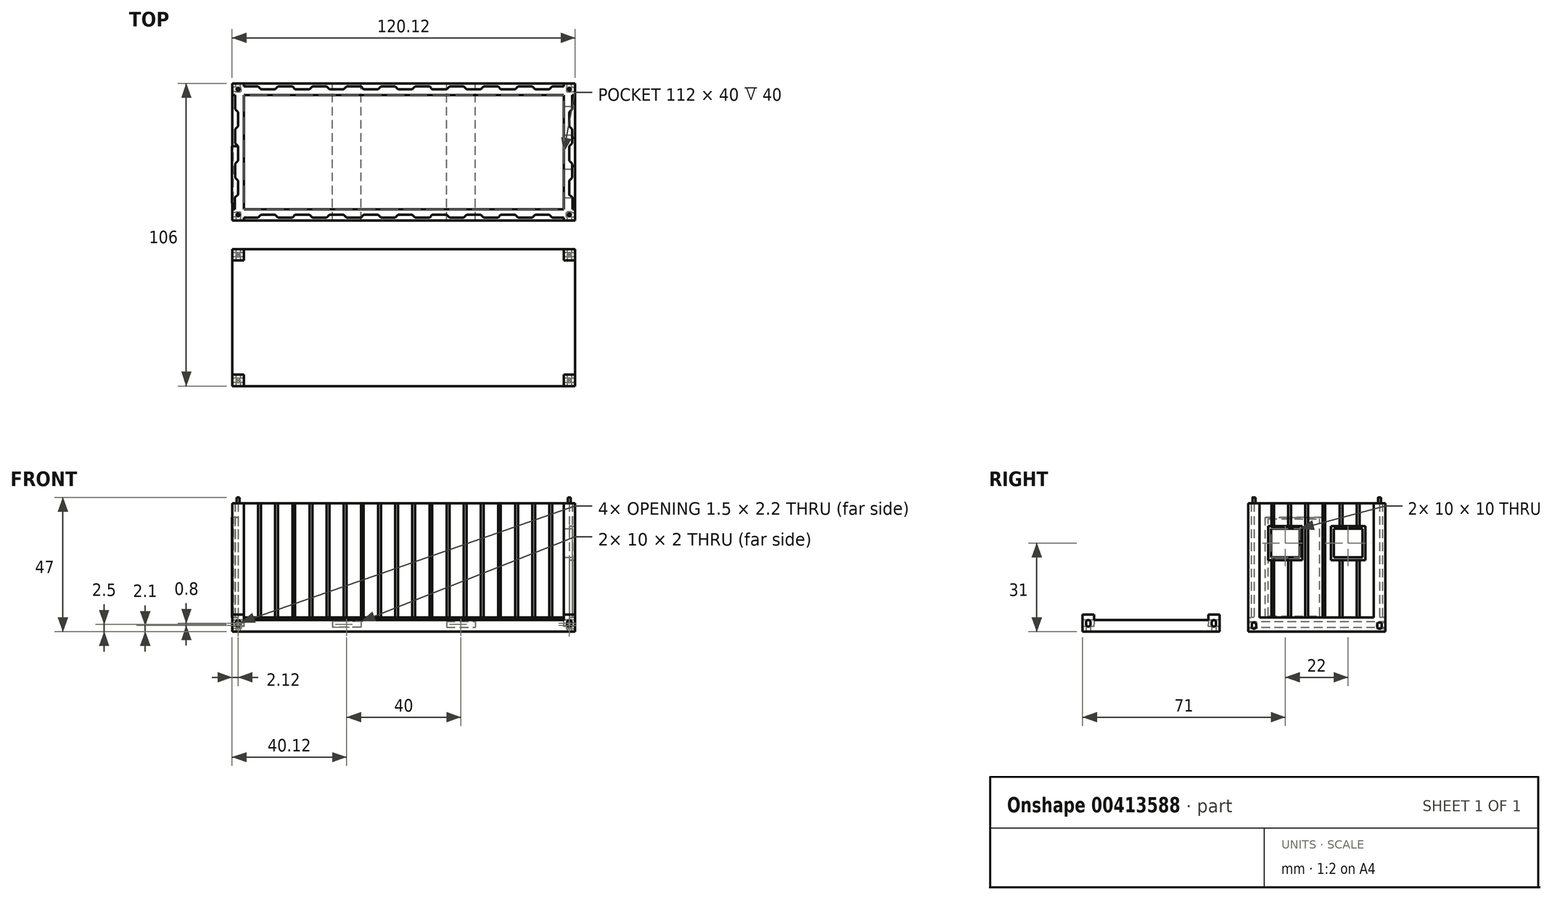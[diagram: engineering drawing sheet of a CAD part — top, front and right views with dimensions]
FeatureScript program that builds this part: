
annotation { "Feature Type Name" : "Feature", "Feature Type Description" : "" }
export const myFeature = defineFeature(function(context is Context, id is Id, definition is map)
    precondition{}
    {
        {
            var Q0;
            Q0=qCreatedBy(makeId("Top.planeOp"),FACE);
            var sketch = newSketch(context, id + "F0", { "sketchPlane" : qUnion([Q0])});
            skLineSegment(sketch, "E0.bottom", {"start": v(0, 0) * mm, "end": v(120, 0) * mm});
            skLineSegment(sketch, "E0.top", {"start": v(0, 48) * mm, "end": v(120, 48) * mm});
            skLineSegment(sketch, "E0.left", {"start": v(0, 0) * mm, "end": v(0, 48) * mm});
            skLineSegment(sketch, "E0.right", {"start": v(120, 0) * mm, "end": v(120, 48) * mm});
            skSolve(sketch);
        }
        {
            var Q0;
            Q0=makeQuery(id+"F0.imprint","IMPRINT",FACE,{"disambiguationData":[TD([[makeQuery(id+"F0.imprint","IMPRINT",EDGE,{"derivedFrom":sQuery(id+"F0.wireOp",EDGE,"E0.bottom")}),1.0]])]});
            extrude(context, id + "F1", {"entities" : qUnion([Q0]), "depth" : 5 * mm});
        }
        {
            var Q0;
            Q0=makeQuery(id+"F1.opExtrude","CAP_FACE",FACE,{"disambiguationData":[OSD([sQuery(id+"F0.wireOp",EDGE,"E0.bottom"),sQuery(id+"F0.wireOp",EDGE,"E0.top"),sQuery(id+"F0.wireOp",EDGE,"E0.left"),sQuery(id+"F0.wireOp",EDGE,"E0.right")])],"isStart":false});
            var sketch = newSketch(context, id + "F2", { "sketchPlane" : qUnion([Q0])});
            skLineSegment(sketch, "E1.bottom", {"start": v(120, 48) * mm, "end": v(116, 48) * mm});
            skLineSegment(sketch, "E1.top", {"start": v(120, 44) * mm, "end": v(119, 44) * mm});
            skLineSegment(sketch, "E1.left", {"start": v(120, 48) * mm, "end": v(120, 44) * mm});
            skLineSegment(sketch, "E1.right", {"start": v(116, 48) * mm, "end": v(116, 47) * mm});
            skLineSegment(sketch, "E2.bottom", {"start": v(120, 0) * mm, "end": v(116, 0) * mm});
            skLineSegment(sketch, "E2.top", {"start": v(120, 4) * mm, "end": v(119.12, 4) * mm});
            skLineSegment(sketch, "E2.left", {"start": v(120, 0) * mm, "end": v(120, 4) * mm});
            skLineSegment(sketch, "E2.right", {"start": v(116, 0) * mm, "end": v(116, 1) * mm});
            skLineSegment(sketch, "E3.bottom", {"start": v(0, 48) * mm, "end": v(4, 48) * mm});
            skLineSegment(sketch, "E3.top", {"start": v(0, 44) * mm, "end": v(1, 44) * mm});
            skLineSegment(sketch, "E3.left", {"start": v(0, 48) * mm, "end": v(0, 44) * mm});
            skLineSegment(sketch, "E3.right", {"start": v(4, 48) * mm, "end": v(4, 47) * mm});
            skLineSegment(sketch, "E4.bottom", {"start": v(0, 0) * mm, "end": v(4, 0) * mm});
            skLineSegment(sketch, "E4.top", {"start": v(0, 4) * mm, "end": v(0.88, 4) * mm});
            skLineSegment(sketch, "E4.left", {"start": v(0, 0) * mm, "end": v(0, 4) * mm});
            skLineSegment(sketch, "E4.right", {"start": v(4, 0) * mm, "end": v(4, 1) * mm});
            skLineSegment(sketch, "E5", {"start": v(4, 48) * mm, "end": v(4, 47) * mm, "construction": true});
            skLineSegment(sketch, "E6", {"start": v(4, 47) * mm, "end": v(9, 47) * mm});
            skLineSegment(sketch, "E7", {"start": v(9, 47) * mm, "end": v(10, 46) * mm});
            skLineSegment(sketch, "E8", {"start": v(10, 46) * mm, "end": v(15, 46) * mm});
            skLineSegment(sketch, "E9", {"start": v(15, 46) * mm, "end": v(16, 47) * mm});
            skLineSegment(sketch, "E10.1.0.0", {"start": v(16, 47) * mm, "end": v(21, 47) * mm});
            skLineSegment(sketch, "E10.1.0.1", {"start": v(21, 47) * mm, "end": v(22, 46) * mm});
            skLineSegment(sketch, "E10.1.0.2", {"start": v(27, 46) * mm, "end": v(28, 47) * mm});
            skLineSegment(sketch, "E10.2.0.0", {"start": v(28, 47) * mm, "end": v(33, 47) * mm});
            skLineSegment(sketch, "E10.2.0.1", {"start": v(33, 47) * mm, "end": v(34, 46) * mm});
            skLineSegment(sketch, "E10.2.0.2", {"start": v(39, 46) * mm, "end": v(40, 47) * mm});
            skLineSegment(sketch, "E10.3.0.0", {"start": v(40, 47) * mm, "end": v(45, 47) * mm});
            skLineSegment(sketch, "E10.3.0.1", {"start": v(45, 47) * mm, "end": v(46, 46) * mm});
            skLineSegment(sketch, "E10.3.0.2", {"start": v(51, 46) * mm, "end": v(52, 47) * mm});
            skLineSegment(sketch, "E10.4.0.0", {"start": v(52, 47) * mm, "end": v(57, 47) * mm});
            skLineSegment(sketch, "E10.4.0.1", {"start": v(57, 47) * mm, "end": v(58, 46) * mm});
            skLineSegment(sketch, "E10.4.0.2", {"start": v(63, 46) * mm, "end": v(64, 47) * mm});
            skLineSegment(sketch, "E10.5.0.0", {"start": v(64, 47) * mm, "end": v(69, 47) * mm});
            skLineSegment(sketch, "E10.5.0.1", {"start": v(69, 47) * mm, "end": v(70, 46) * mm});
            skLineSegment(sketch, "E10.5.0.2", {"start": v(75, 46) * mm, "end": v(76, 47) * mm});
            skLineSegment(sketch, "E10.6.0.0", {"start": v(76, 47) * mm, "end": v(81, 47) * mm});
            skLineSegment(sketch, "E10.6.0.1", {"start": v(81, 47) * mm, "end": v(82, 46) * mm});
            skLineSegment(sketch, "E10.6.0.2", {"start": v(87, 46) * mm, "end": v(88, 47) * mm});
            skLineSegment(sketch, "E10.7.0.0", {"start": v(88, 47) * mm, "end": v(93, 47) * mm});
            skLineSegment(sketch, "E10.7.0.1", {"start": v(93, 47) * mm, "end": v(94, 46) * mm});
            skLineSegment(sketch, "E10.7.0.2", {"start": v(99, 46) * mm, "end": v(100, 47) * mm});
            skLineSegment(sketch, "E10.8.0.0", {"start": v(100, 47) * mm, "end": v(105, 47) * mm});
            skLineSegment(sketch, "E10.8.0.1", {"start": v(105, 47) * mm, "end": v(106, 46) * mm});
            skLineSegment(sketch, "E10.8.0.2", {"start": v(111, 46) * mm, "end": v(112, 47) * mm});
            skLineSegment(sketch, "E11", {"start": v(112, 47) * mm, "end": v(116, 47) * mm});
            skLineSegment(sketch, "E12", {"start": v(22, 46) * mm, "end": v(27, 46) * mm});
            skLineSegment(sketch, "E13", {"start": v(34, 46) * mm, "end": v(39, 46) * mm});
            skLineSegment(sketch, "E14", {"start": v(46, 46) * mm, "end": v(51, 46) * mm});
            skLineSegment(sketch, "E15", {"start": v(58, 46) * mm, "end": v(63, 46) * mm});
            skLineSegment(sketch, "E16", {"start": v(70, 46) * mm, "end": v(75, 46) * mm});
            skLineSegment(sketch, "E17", {"start": v(82, 46) * mm, "end": v(87, 46) * mm});
            skLineSegment(sketch, "E18", {"start": v(94, 46) * mm, "end": v(99, 46) * mm});
            skLineSegment(sketch, "E19", {"start": v(106, 46) * mm, "end": v(111, 46) * mm});
            skLineSegment(sketch, "E20", {"start": v(4, 44) * mm, "end": v(116, 44) * mm});
            skLineSegment(sketch, "E21.MirrorCS", {"start": v(4, 1) * mm, "end": v(9, 1) * mm});
            skLineSegment(sketch, "E22.MirrorCS", {"start": v(9, 1) * mm, "end": v(10, 2) * mm});
            skLineSegment(sketch, "E23.MirrorCS", {"start": v(10, 2) * mm, "end": v(15, 2) * mm});
            skLineSegment(sketch, "E24.MirrorCS", {"start": v(15, 2) * mm, "end": v(16, 1) * mm});
            skLineSegment(sketch, "E25.MirrorCS", {"start": v(16, 1) * mm, "end": v(21, 1) * mm});
            skLineSegment(sketch, "E26.MirrorCS", {"start": v(21, 1) * mm, "end": v(22, 2) * mm});
            skLineSegment(sketch, "E27.MirrorCS", {"start": v(22, 2) * mm, "end": v(27, 2) * mm});
            skLineSegment(sketch, "E28.MirrorCS", {"start": v(27, 2) * mm, "end": v(28, 1) * mm});
            skLineSegment(sketch, "E29.MirrorCS", {"start": v(28, 1) * mm, "end": v(33, 1) * mm});
            skLineSegment(sketch, "E30.MirrorCS", {"start": v(33, 1) * mm, "end": v(34, 2) * mm});
            skLineSegment(sketch, "E31.MirrorCS", {"start": v(34, 2) * mm, "end": v(39, 2) * mm});
            skLineSegment(sketch, "E32.MirrorCS", {"start": v(39, 2) * mm, "end": v(40, 1) * mm});
            skLineSegment(sketch, "E33.MirrorCS", {"start": v(40, 1) * mm, "end": v(45, 1) * mm});
            skLineSegment(sketch, "E34.MirrorCS", {"start": v(45, 1) * mm, "end": v(46, 2) * mm});
            skLineSegment(sketch, "E35.MirrorCS", {"start": v(46, 2) * mm, "end": v(51, 2) * mm});
            skLineSegment(sketch, "E36.MirrorCS", {"start": v(51, 2) * mm, "end": v(52, 1) * mm});
            skLineSegment(sketch, "E37.MirrorCS", {"start": v(52, 1) * mm, "end": v(57, 1) * mm});
            skLineSegment(sketch, "E38.MirrorCS", {"start": v(57, 1) * mm, "end": v(58, 2) * mm});
            skLineSegment(sketch, "E39.MirrorCS", {"start": v(58, 2) * mm, "end": v(63, 2) * mm});
            skLineSegment(sketch, "E40.MirrorCS", {"start": v(63, 2) * mm, "end": v(64, 1) * mm});
            skLineSegment(sketch, "E41.MirrorCS", {"start": v(64, 1) * mm, "end": v(69, 1) * mm});
            skLineSegment(sketch, "E42.MirrorCS", {"start": v(69, 1) * mm, "end": v(70, 2) * mm});
            skLineSegment(sketch, "E43.MirrorCS", {"start": v(70, 2) * mm, "end": v(75, 2) * mm});
            skLineSegment(sketch, "E44.MirrorCS", {"start": v(75, 2) * mm, "end": v(76, 1) * mm});
            skLineSegment(sketch, "E45.MirrorCS", {"start": v(76, 1) * mm, "end": v(81, 1) * mm});
            skLineSegment(sketch, "E46.MirrorCS", {"start": v(81, 1) * mm, "end": v(82, 2) * mm});
            skLineSegment(sketch, "E47.MirrorCS", {"start": v(82, 2) * mm, "end": v(87, 2) * mm});
            skLineSegment(sketch, "E48.MirrorCS", {"start": v(87, 2) * mm, "end": v(88, 1) * mm});
            skLineSegment(sketch, "E49.MirrorCS", {"start": v(88, 1) * mm, "end": v(93, 1) * mm});
            skLineSegment(sketch, "E50.MirrorCS", {"start": v(93, 1) * mm, "end": v(94, 2) * mm});
            skLineSegment(sketch, "E51.MirrorCS", {"start": v(94, 2) * mm, "end": v(99, 2) * mm});
            skLineSegment(sketch, "E52.MirrorCS", {"start": v(99, 2) * mm, "end": v(100, 1) * mm});
            skLineSegment(sketch, "E53.MirrorCS", {"start": v(100, 1) * mm, "end": v(105, 1) * mm});
            skLineSegment(sketch, "E54.MirrorCS", {"start": v(105, 1) * mm, "end": v(106, 2) * mm});
            skLineSegment(sketch, "E55.MirrorCS", {"start": v(106, 2) * mm, "end": v(111, 2) * mm});
            skLineSegment(sketch, "E56.MirrorCS", {"start": v(111, 2) * mm, "end": v(112, 1) * mm});
            skLineSegment(sketch, "E57.MirrorCS", {"start": v(112, 1) * mm, "end": v(116, 1) * mm});
            skLineSegment(sketch, "E58", {"start": v(4, 4) * mm, "end": v(116, 4) * mm});
            skLineSegment(sketch, "E59", {"start": v(0, 44) * mm, "end": v(1, 44) * mm, "construction": true});
            skLineSegment(sketch, "E60", {"start": v(1, 44) * mm, "end": v(1, 39) * mm});
            skLineSegment(sketch, "E61", {"start": v(1, 39) * mm, "end": v(2, 38) * mm});
            skLineSegment(sketch, "E62", {"start": v(2, 38) * mm, "end": v(2, 33) * mm});
            skLineSegment(sketch, "E63", {"start": v(2, 33) * mm, "end": v(1, 32) * mm});
            skLineSegment(sketch, "E64", {"start": v(1, 32) * mm, "end": v(1, 27) * mm});
            skLineSegment(sketch, "E65", {"start": v(1, 27) * mm, "end": v(2, 26) * mm});
            skLineSegment(sketch, "E66", {"start": v(2, 26) * mm, "end": v(2, 21) * mm});
            skLineSegment(sketch, "E67", {"start": v(2, 21) * mm, "end": v(1, 20) * mm});
            skLineSegment(sketch, "E68", {"start": v(1, 20) * mm, "end": v(1, 15) * mm});
            skLineSegment(sketch, "E69", {"start": v(1, 15) * mm, "end": v(2.02, 13.98) * mm});
            skLineSegment(sketch, "E70", {"start": v(2.02, 13.98) * mm, "end": v(2.02, 8.98) * mm});
            skLineSegment(sketch, "E71", {"start": v(2.02, 8.98) * mm, "end": v(0.88, 8.1) * mm});
            skLineSegment(sketch, "E72", {"start": v(0.88, 8.1) * mm, "end": v(0.88, 4) * mm});
            skLineSegment(sketch, "E73.MirrorCS", {"start": v(119.12, 8.1) * mm, "end": v(119.12, 4) * mm});
            skLineSegment(sketch, "E74.MirrorCS", {"start": v(117.98, 8.98) * mm, "end": v(119.12, 8.1) * mm});
            skLineSegment(sketch, "E75.MirrorCS", {"start": v(117.98, 13.98) * mm, "end": v(117.98, 8.98) * mm});
            skLineSegment(sketch, "E76.MirrorCS", {"start": v(119, 15) * mm, "end": v(117.98, 13.98) * mm});
            skLineSegment(sketch, "E77.MirrorCS", {"start": v(119, 20) * mm, "end": v(119, 15) * mm});
            skLineSegment(sketch, "E78.MirrorCS", {"start": v(118, 21) * mm, "end": v(119, 20) * mm});
            skLineSegment(sketch, "E79.MirrorCS", {"start": v(118, 26) * mm, "end": v(118, 21) * mm});
            skLineSegment(sketch, "E80.MirrorCS", {"start": v(119, 32) * mm, "end": v(119, 27) * mm});
            skLineSegment(sketch, "E81.MirrorCS", {"start": v(118, 33) * mm, "end": v(119, 32) * mm});
            skLineSegment(sketch, "E82.MirrorCS", {"start": v(118, 38) * mm, "end": v(118, 33) * mm});
            skLineSegment(sketch, "E83.MirrorCS", {"start": v(119, 39) * mm, "end": v(118, 38) * mm});
            skLineSegment(sketch, "E84.MirrorCS", {"start": v(119, 44) * mm, "end": v(119, 39) * mm});
            skLineSegment(sketch, "E85.MirrorCS", {"start": v(119, 27) * mm, "end": v(118, 26) * mm});
            skLineSegment(sketch, "E86", {"start": v(4, 44) * mm, "end": v(4, 4) * mm});
            skLineSegment(sketch, "E87", {"start": v(116, 4) * mm, "end": v(116, 44) * mm});
            skPoint(sketch, "E88.orphan", {"position": v(4, 46) * mm});
            skPoint(sketch, "E89.orphan", {"position": v(2, 44) * mm});
            skSolve(sketch);
        }
        {
            var Q0;
            Q0 = qSketchRegion(id + "F2", true);
            extrude(context, id + "F3", {"entities" : qUnion([Q0]), "operationType" : NewBodyOperationType.ADD, "depth" : 40 * mm});
        }
        {
            var Q0;
            Q0=makeQuery(id+"F3.opExtrude","CAP_FACE",FACE,{"disambiguationData":[OSD([sQuery(id+"F2.wireOp",EDGE,"E1.bottom"),sQuery(id+"F2.wireOp",EDGE,"E1.top"),sQuery(id+"F2.wireOp",EDGE,"E1.left"),sQuery(id+"F2.wireOp",EDGE,"E1.right"),sQuery(id+"F2.wireOp",EDGE,"E2.bottom"),sQuery(id+"F2.wireOp",EDGE,"E2.top"),sQuery(id+"F2.wireOp",EDGE,"E2.left"),sQuery(id+"F2.wireOp",EDGE,"E2.right"),sQuery(id+"F2.wireOp",EDGE,"E3.bottom"),sQuery(id+"F2.wireOp",EDGE,"E3.top"),sQuery(id+"F2.wireOp",EDGE,"E3.left"),sQuery(id+"F2.wireOp",EDGE,"E3.right"),sQuery(id+"F2.wireOp",EDGE,"E4.bottom"),sQuery(id+"F2.wireOp",EDGE,"E4.top"),sQuery(id+"F2.wireOp",EDGE,"E4.left"),sQuery(id+"F2.wireOp",EDGE,"E4.right"),sQuery(id+"F2.wireOp",EDGE,"E6"),sQuery(id+"F2.wireOp",EDGE,"E7"),sQuery(id+"F2.wireOp",EDGE,"E8"),sQuery(id+"F2.wireOp",EDGE,"E9"),sQuery(id+"F2.wireOp",EDGE,"E10.1.0.0"),sQuery(id+"F2.wireOp",EDGE,"E10.1.0.1"),sQuery(id+"F2.wireOp",EDGE,"E10.1.0.2"),sQuery(id+"F2.wireOp",EDGE,"E10.2.0.0"),sQuery(id+"F2.wireOp",EDGE,"E10.2.0.1"),sQuery(id+"F2.wireOp",EDGE,"E10.2.0.2"),sQuery(id+"F2.wireOp",EDGE,"E10.3.0.0"),sQuery(id+"F2.wireOp",EDGE,"E10.3.0.1"),sQuery(id+"F2.wireOp",EDGE,"E10.3.0.2"),sQuery(id+"F2.wireOp",EDGE,"E10.4.0.0"),sQuery(id+"F2.wireOp",EDGE,"E10.4.0.1"),sQuery(id+"F2.wireOp",EDGE,"E10.4.0.2"),sQuery(id+"F2.wireOp",EDGE,"E10.5.0.0"),sQuery(id+"F2.wireOp",EDGE,"E10.5.0.1"),sQuery(id+"F2.wireOp",EDGE,"E10.5.0.2"),sQuery(id+"F2.wireOp",EDGE,"E10.6.0.0"),sQuery(id+"F2.wireOp",EDGE,"E10.6.0.1"),sQuery(id+"F2.wireOp",EDGE,"E10.6.0.2"),sQuery(id+"F2.wireOp",EDGE,"E10.7.0.0"),sQuery(id+"F2.wireOp",EDGE,"E10.7.0.1"),sQuery(id+"F2.wireOp",EDGE,"E10.7.0.2"),sQuery(id+"F2.wireOp",EDGE,"E10.8.0.0"),sQuery(id+"F2.wireOp",EDGE,"E10.8.0.1"),sQuery(id+"F2.wireOp",EDGE,"E10.8.0.2"),sQuery(id+"F2.wireOp",EDGE,"E11"),sQuery(id+"F2.wireOp",EDGE,"E12"),sQuery(id+"F2.wireOp",EDGE,"E13"),sQuery(id+"F2.wireOp",EDGE,"E14"),sQuery(id+"F2.wireOp",EDGE,"E15"),sQuery(id+"F2.wireOp",EDGE,"E16"),sQuery(id+"F2.wireOp",EDGE,"E17"),sQuery(id+"F2.wireOp",EDGE,"E18"),sQuery(id+"F2.wireOp",EDGE,"E19"),sQuery(id+"F2.wireOp",EDGE,"E20"),sQuery(id+"F2.wireOp",EDGE,"E21.MirrorCS"),sQuery(id+"F2.wireOp",EDGE,"E22.MirrorCS"),sQuery(id+"F2.wireOp",EDGE,"E23.MirrorCS"),sQuery(id+"F2.wireOp",EDGE,"E24.MirrorCS"),sQuery(id+"F2.wireOp",EDGE,"E25.MirrorCS"),sQuery(id+"F2.wireOp",EDGE,"E26.MirrorCS"),sQuery(id+"F2.wireOp",EDGE,"E27.MirrorCS"),sQuery(id+"F2.wireOp",EDGE,"E28.MirrorCS"),sQuery(id+"F2.wireOp",EDGE,"E29.MirrorCS"),sQuery(id+"F2.wireOp",EDGE,"E30.MirrorCS"),sQuery(id+"F2.wireOp",EDGE,"E31.MirrorCS"),sQuery(id+"F2.wireOp",EDGE,"E32.MirrorCS"),sQuery(id+"F2.wireOp",EDGE,"E33.MirrorCS"),sQuery(id+"F2.wireOp",EDGE,"E34.MirrorCS"),sQuery(id+"F2.wireOp",EDGE,"E35.MirrorCS"),sQuery(id+"F2.wireOp",EDGE,"E36.MirrorCS"),sQuery(id+"F2.wireOp",EDGE,"E37.MirrorCS"),sQuery(id+"F2.wireOp",EDGE,"E38.MirrorCS"),sQuery(id+"F2.wireOp",EDGE,"E39.MirrorCS"),sQuery(id+"F2.wireOp",EDGE,"E40.MirrorCS"),sQuery(id+"F2.wireOp",EDGE,"E41.MirrorCS"),sQuery(id+"F2.wireOp",EDGE,"E42.MirrorCS"),sQuery(id+"F2.wireOp",EDGE,"E43.MirrorCS"),sQuery(id+"F2.wireOp",EDGE,"E44.MirrorCS"),sQuery(id+"F2.wireOp",EDGE,"E45.MirrorCS"),sQuery(id+"F2.wireOp",EDGE,"E46.MirrorCS"),sQuery(id+"F2.wireOp",EDGE,"E47.MirrorCS"),sQuery(id+"F2.wireOp",EDGE,"E48.MirrorCS"),sQuery(id+"F2.wireOp",EDGE,"E49.MirrorCS"),sQuery(id+"F2.wireOp",EDGE,"E50.MirrorCS"),sQuery(id+"F2.wireOp",EDGE,"E51.MirrorCS"),sQuery(id+"F2.wireOp",EDGE,"E52.MirrorCS"),sQuery(id+"F2.wireOp",EDGE,"E53.MirrorCS"),sQuery(id+"F2.wireOp",EDGE,"E54.MirrorCS"),sQuery(id+"F2.wireOp",EDGE,"E55.MirrorCS"),sQuery(id+"F2.wireOp",EDGE,"E56.MirrorCS"),sQuery(id+"F2.wireOp",EDGE,"E57.MirrorCS"),sQuery(id+"F2.wireOp",EDGE,"E58"),sQuery(id+"F2.wireOp",EDGE,"E60"),sQuery(id+"F2.wireOp",EDGE,"E61"),sQuery(id+"F2.wireOp",EDGE,"E62"),sQuery(id+"F2.wireOp",EDGE,"E63"),sQuery(id+"F2.wireOp",EDGE,"E64"),sQuery(id+"F2.wireOp",EDGE,"E65"),sQuery(id+"F2.wireOp",EDGE,"E66"),sQuery(id+"F2.wireOp",EDGE,"E67"),sQuery(id+"F2.wireOp",EDGE,"E68"),sQuery(id+"F2.wireOp",EDGE,"E69"),sQuery(id+"F2.wireOp",EDGE,"E70"),sQuery(id+"F2.wireOp",EDGE,"E71"),sQuery(id+"F2.wireOp",EDGE,"E72"),sQuery(id+"F2.wireOp",EDGE,"E73.MirrorCS"),sQuery(id+"F2.wireOp",EDGE,"E74.MirrorCS"),sQuery(id+"F2.wireOp",EDGE,"E75.MirrorCS"),sQuery(id+"F2.wireOp",EDGE,"E76.MirrorCS"),sQuery(id+"F2.wireOp",EDGE,"E77.MirrorCS"),sQuery(id+"F2.wireOp",EDGE,"E78.MirrorCS"),sQuery(id+"F2.wireOp",EDGE,"E79.MirrorCS"),sQuery(id+"F2.wireOp",EDGE,"E80.MirrorCS"),sQuery(id+"F2.wireOp",EDGE,"E81.MirrorCS"),sQuery(id+"F2.wireOp",EDGE,"E82.MirrorCS"),sQuery(id+"F2.wireOp",EDGE,"E83.MirrorCS"),sQuery(id+"F2.wireOp",EDGE,"E84.MirrorCS"),sQuery(id+"F2.wireOp",EDGE,"E85.MirrorCS"),sQuery(id+"F2.wireOp",EDGE,"E86"),sQuery(id+"F2.wireOp",EDGE,"E87")])],"isStart":false});
            var sketch = newSketch(context, id + "F4", { "sketchPlane" : qUnion([Q0])});
            skLineSegment(sketch, "E90.bottom", {"start": v(0, 0) * mm, "end": v(120, 0) * mm});
            skLineSegment(sketch, "E90.top", {"start": v(0, 48) * mm, "end": v(120, 48) * mm});
            skLineSegment(sketch, "E90.left", {"start": v(0, 0) * mm, "end": v(0, 48) * mm});
            skLineSegment(sketch, "E90.right", {"start": v(120, 0) * mm, "end": v(120, 48) * mm});
            skSolve(sketch);
        }
        {
            var Q0;
            Q0 = qSketchRegion(id + "F4", true);
            extrude(context, id + "F5", {"entities" : qUnion([Q0]), "operationType" : NewBodyOperationType.ADD, "depth" : 3 * mm});
        }
        {
            var Q0;
            Q0=makeQuery(id+"F5.opExtrude","CAP_FACE",FACE,{"disambiguationData":[OSD([sQuery(id+"F4.wireOp",EDGE,"E90.bottom"),sQuery(id+"F4.wireOp",EDGE,"E90.top"),sQuery(id+"F4.wireOp",EDGE,"E90.left"),sQuery(id+"F4.wireOp",EDGE,"E90.right")])],"isStart":false});
            var sketch = newSketch(context, id + "F6", { "sketchPlane" : qUnion([Q0])});
            skLineSegment(sketch, "E91.bottom", {"start": v(0, 48) * mm, "end": v(4, 48) * mm});
            skLineSegment(sketch, "E91.top", {"start": v(0, 44) * mm, "end": v(4, 44) * mm});
            skLineSegment(sketch, "E91.left", {"start": v(0, 48) * mm, "end": v(0, 44) * mm});
            skLineSegment(sketch, "E91.right", {"start": v(4, 48) * mm, "end": v(4, 44) * mm});
            skLineSegment(sketch, "E92.bottom", {"start": v(0, 0) * mm, "end": v(4, 0) * mm});
            skLineSegment(sketch, "E92.top", {"start": v(0, 4) * mm, "end": v(4, 4) * mm});
            skLineSegment(sketch, "E92.left", {"start": v(0, 0) * mm, "end": v(0, 4) * mm});
            skLineSegment(sketch, "E92.right", {"start": v(4, 0) * mm, "end": v(4, 4) * mm});
            skLineSegment(sketch, "E93.bottom", {"start": v(120, 48) * mm, "end": v(116, 48) * mm});
            skLineSegment(sketch, "E93.top", {"start": v(120, 44) * mm, "end": v(116, 44) * mm});
            skLineSegment(sketch, "E93.left", {"start": v(120, 48) * mm, "end": v(120, 44) * mm});
            skLineSegment(sketch, "E93.right", {"start": v(116, 48) * mm, "end": v(116, 44) * mm});
            skLineSegment(sketch, "E94.bottom", {"start": v(120, 0) * mm, "end": v(116, 0) * mm});
            skLineSegment(sketch, "E94.top", {"start": v(120, 4) * mm, "end": v(116, 4) * mm});
            skLineSegment(sketch, "E94.left", {"start": v(120, 0) * mm, "end": v(120, 4) * mm});
            skLineSegment(sketch, "E94.right", {"start": v(116, 0) * mm, "end": v(116, 4) * mm});
            skSolve(sketch);
        }
        {
            var Q0;
            Q0 = qSketchRegion(id + "F6", true);
            extrude(context, id + "F7", {"entities" : qUnion([Q0]), "operationType" : NewBodyOperationType.ADD, "depth" : 2 * mm});
        }
        {
            var Q0;
            Q0=makeQuery(id+"F7.boolean.opBoolean","MERGE",FACE,{"derivedFrom":[makeQuery(id+"F5.boolean.opBoolean","MERGE",FACE,{"derivedFrom":[makeQuery(id+"F3.boolean.opBoolean","MERGE",FACE,{"derivedFrom":[makeQuery(id+"F1.opExtrude","SWEPT_FACE",FACE,{"disambiguationData":[OSD([sQuery(id+"F0.wireOp",EDGE,"E0.bottom")])]}),makeQuery(id+"F3.opExtrude","SWEPT_FACE",FACE,{"disambiguationData":[OSD([sQuery(id+"F2.wireOp",EDGE,"E2.bottom")])]}),makeQuery(id+"F3.opExtrude","SWEPT_FACE",FACE,{"disambiguationData":[OSD([sQuery(id+"F2.wireOp",EDGE,"E4.bottom")])]})]}),makeQuery(id+"F5.opExtrude","SWEPT_FACE",FACE,{"disambiguationData":[OSD([sQuery(id+"F4.wireOp",EDGE,"E90.bottom")])]})]}),makeQuery(id+"F7.opExtrude","SWEPT_FACE",FACE,{"disambiguationData":[OSD([sQuery(id+"F6.wireOp",EDGE,"E92.bottom")])]}),makeQuery(id+"F7.opExtrude","SWEPT_FACE",FACE,{"disambiguationData":[OSD([sQuery(id+"F6.wireOp",EDGE,"E94.bottom")])]})]});
            var sketch = newSketch(context, id + "F8", { "sketchPlane" : qUnion([Q0])});
            skLineSegment(sketch, "E95", {"start": v(2, 50) * mm, "end": v(1.25, 50) * mm, "construction": true});
            skLineSegment(sketch, "E96", {"start": v(1.25, 50) * mm, "end": v(1.25, 49) * mm, "construction": true});
            skLineSegment(sketch, "E97.bottom", {"start": v(1.95, 49) * mm, "end": v(2.05, 49) * mm});
            skLineSegment(sketch, "E97.top", {"start": v(1.95, 46.8) * mm, "end": v(2.05, 46.8) * mm});
            skLineSegment(sketch, "E97.left", {"start": v(1.25, 48.3) * mm, "end": v(1.25, 47.5) * mm});
            skLineSegment(sketch, "E97.right", {"start": v(2.75, 48.3) * mm, "end": v(2.75, 47.5) * mm});
            skPoint(sketch, "E98.visualSharp", {"position": v(1.25, 49) * mm});
            skArc(sketch, "E98.filletArc", {"start": v(1.95, 49) * mm, "mid": v(1.46, 48.8) * mm, "end": v(1.25, 48.3) * mm});
            skPoint(sketch, "E99.visualSharp", {"position": v(2.75, 49) * mm});
            skArc(sketch, "E99.filletArc", {"start": v(2.75, 48.3) * mm, "mid": v(2.54, 48.8) * mm, "end": v(2.05, 49) * mm});
            skPoint(sketch, "E100.visualSharp", {"position": v(1.25, 46.8) * mm});
            skArc(sketch, "E100.filletArc", {"start": v(1.25, 47.5) * mm, "mid": v(1.46, 47) * mm, "end": v(1.95, 46.8) * mm});
            skPoint(sketch, "E101.visualSharp", {"position": v(2.75, 46.8) * mm});
            skArc(sketch, "E101.filletArc", {"start": v(2.05, 46.8) * mm, "mid": v(2.54, 47) * mm, "end": v(2.75, 47.5) * mm});
            skLineSegment(sketch, "E102", {"start": v(60, 48) * mm, "end": v(60, 62.26) * mm, "construction": true});
            skPoint(sketch, "E102.endSnap0", {"position": v(60, 45) * mm});
            skArc(sketch, "E103.MirrorCS", {"start": v(118.05, 49) * mm, "mid": v(118.54, 48.8) * mm, "end": v(118.75, 48.3) * mm});
            skLineSegment(sketch, "E104.MirrorCS", {"start": v(118.05, 49) * mm, "end": v(117.95, 49) * mm});
            skArc(sketch, "E105.MirrorCS", {"start": v(117.25, 48.3) * mm, "mid": v(117.46, 48.8) * mm, "end": v(117.95, 49) * mm});
            skLineSegment(sketch, "E106.MirrorCS", {"start": v(118.75, 48.3) * mm, "end": v(118.75, 47.5) * mm});
            skArc(sketch, "E107.MirrorCS", {"start": v(118.75, 47.5) * mm, "mid": v(118.54, 47) * mm, "end": v(118.05, 46.8) * mm});
            skLineSegment(sketch, "E108.MirrorCS", {"start": v(117.25, 48.3) * mm, "end": v(117.25, 47.5) * mm});
            skArc(sketch, "E109.MirrorCS", {"start": v(117.95, 46.8) * mm, "mid": v(117.46, 47) * mm, "end": v(117.25, 47.5) * mm});
            skLineSegment(sketch, "E110.MirrorCS", {"start": v(118.05, 46.8) * mm, "end": v(117.95, 46.8) * mm});
            skLineSegment(sketch, "E111", {"start": v(0, 25) * mm, "end": v(-2.77, 25) * mm, "construction": true});
            skLineSegment(sketch, "E112.MirrorCS", {"start": v(1.25, 1.7) * mm, "end": v(1.25, 2.5) * mm});
            skArc(sketch, "E113.MirrorCS", {"start": v(1.95, 1) * mm, "mid": v(1.46, 1.2) * mm, "end": v(1.25, 1.7) * mm});
            skLineSegment(sketch, "E114.MirrorCS", {"start": v(1.95, 1) * mm, "end": v(2.05, 1) * mm});
            skArc(sketch, "E115.MirrorCS", {"start": v(2.75, 1.7) * mm, "mid": v(2.54, 1.2) * mm, "end": v(2.05, 1) * mm});
            skArc(sketch, "E116.MirrorCS", {"start": v(2.05, 3.2) * mm, "mid": v(2.54, 3) * mm, "end": v(2.75, 2.5) * mm});
            skLineSegment(sketch, "E117.MirrorCS", {"start": v(1.95, 3.2) * mm, "end": v(2.05, 3.2) * mm});
            skArc(sketch, "E118.MirrorCS", {"start": v(1.25, 2.5) * mm, "mid": v(1.46, 3) * mm, "end": v(1.95, 3.2) * mm});
            skLineSegment(sketch, "E119.MirrorCS", {"start": v(2.75, 1.7) * mm, "end": v(2.75, 2.5) * mm});
            skLineSegment(sketch, "E120.MirrorCS", {"start": v(117.25, 1.7) * mm, "end": v(117.25, 2.5) * mm});
            skArc(sketch, "E121.MirrorCS", {"start": v(117.25, 1.7) * mm, "mid": v(117.46, 1.2) * mm, "end": v(117.95, 1) * mm});
            skLineSegment(sketch, "E122.MirrorCS", {"start": v(118.05, 1) * mm, "end": v(117.95, 1) * mm});
            skArc(sketch, "E123.MirrorCS", {"start": v(118.05, 1) * mm, "mid": v(118.54, 1.2) * mm, "end": v(118.75, 1.7) * mm});
            skLineSegment(sketch, "E124.MirrorCS", {"start": v(118.75, 1.7) * mm, "end": v(118.75, 2.5) * mm});
            skArc(sketch, "E125.MirrorCS", {"start": v(118.75, 2.5) * mm, "mid": v(118.54, 3) * mm, "end": v(118.05, 3.2) * mm});
            skLineSegment(sketch, "E126.MirrorCS", {"start": v(118.05, 3.2) * mm, "end": v(117.95, 3.2) * mm});
            skArc(sketch, "E127.MirrorCS", {"start": v(117.95, 3.2) * mm, "mid": v(117.46, 3) * mm, "end": v(117.25, 2.5) * mm});
            skSolve(sketch);
        }
        {
            var Q0;
            Q0 = qSketchRegion(id + "F8", true);
            extrude(context, id + "F9", {"entities" : qUnion([Q0]), "operationType" : NewBodyOperationType.REMOVE, "oppositeDirection" : true, "depth" : 3 * mm});
        }
        {
            var Q0;
            Q0=makeQuery(id+"F7.boolean.opBoolean","MERGE",FACE,{"derivedFrom":[makeQuery(id+"F5.boolean.opBoolean","MERGE",FACE,{"derivedFrom":[makeQuery(id+"F3.boolean.opBoolean","MERGE",FACE,{"derivedFrom":[makeQuery(id+"F1.opExtrude","SWEPT_FACE",FACE,{"disambiguationData":[OSD([sQuery(id+"F0.wireOp",EDGE,"E0.right")])]}),makeQuery(id+"F3.opExtrude","SWEPT_FACE",FACE,{"disambiguationData":[OSD([sQuery(id+"F2.wireOp",EDGE,"E1.left")])]}),makeQuery(id+"F3.opExtrude","SWEPT_FACE",FACE,{"disambiguationData":[OSD([sQuery(id+"F2.wireOp",EDGE,"E2.left")])]})]}),makeQuery(id+"F5.opExtrude","SWEPT_FACE",FACE,{"disambiguationData":[OSD([sQuery(id+"F4.wireOp",EDGE,"E90.right")])]})]}),makeQuery(id+"F7.opExtrude","SWEPT_FACE",FACE,{"disambiguationData":[OSD([sQuery(id+"F6.wireOp",EDGE,"E93.left")])]}),makeQuery(id+"F7.opExtrude","SWEPT_FACE",FACE,{"disambiguationData":[OSD([sQuery(id+"F6.wireOp",EDGE,"E94.left")])]})]});
            var sketch = newSketch(context, id + "F10", { "sketchPlane" : qUnion([Q0])});
            skLineSegment(sketch, "E128", {"start": v(2, 50) * mm, "end": v(2, 49) * mm, "construction": true});
            skLineSegment(sketch, "E129", {"start": v(2, 49) * mm, "end": v(1.95, 49) * mm, "construction": true});
            skLineSegment(sketch, "E130.bottom", {"start": v(1.95, 49) * mm, "end": v(2.05, 49) * mm});
            skLineSegment(sketch, "E130.top", {"start": v(1.95, 46.8) * mm, "end": v(2.05, 46.8) * mm});
            skLineSegment(sketch, "E130.left", {"start": v(1.25, 48.3) * mm, "end": v(1.25, 47.5) * mm});
            skLineSegment(sketch, "E130.right", {"start": v(2.75, 48.3) * mm, "end": v(2.75, 47.5) * mm});
            skPoint(sketch, "E131.visualSharp", {"position": v(1.25, 49) * mm});
            skArc(sketch, "E131.filletArc", {"start": v(1.95, 49) * mm, "mid": v(1.46, 48.8) * mm, "end": v(1.25, 48.3) * mm});
            skPoint(sketch, "E132.visualSharp", {"position": v(2.75, 49) * mm});
            skArc(sketch, "E132.filletArc", {"start": v(2.75, 48.3) * mm, "mid": v(2.54, 48.8) * mm, "end": v(2.05, 49) * mm});
            skPoint(sketch, "E133.visualSharp", {"position": v(2.75, 46.8) * mm});
            skArc(sketch, "E133.filletArc", {"start": v(2.05, 46.8) * mm, "mid": v(2.54, 47) * mm, "end": v(2.75, 47.5) * mm});
            skPoint(sketch, "E134.visualSharp", {"position": v(1.25, 46.8) * mm});
            skArc(sketch, "E134.filletArc", {"start": v(1.25, 47.5) * mm, "mid": v(1.46, 47) * mm, "end": v(1.95, 46.8) * mm});
            skLineSegment(sketch, "E135", {"start": v(24, 48) * mm, "end": v(24, 52.07) * mm, "construction": true});
            skArc(sketch, "E136.MirrorCS", {"start": v(45.25, 48.3) * mm, "mid": v(45.46, 48.8) * mm, "end": v(45.95, 49) * mm});
            skLineSegment(sketch, "E137.MirrorCS", {"start": v(46.05, 49) * mm, "end": v(45.95, 49) * mm});
            skArc(sketch, "E138.MirrorCS", {"start": v(46.05, 49) * mm, "mid": v(46.54, 48.8) * mm, "end": v(46.75, 48.3) * mm});
            skLineSegment(sketch, "E139.MirrorCS", {"start": v(46.75, 48.3) * mm, "end": v(46.75, 47.5) * mm});
            skArc(sketch, "E140.MirrorCS", {"start": v(46.75, 47.5) * mm, "mid": v(46.54, 47) * mm, "end": v(46.05, 46.8) * mm});
            skLineSegment(sketch, "E141.MirrorCS", {"start": v(46.05, 46.8) * mm, "end": v(45.95, 46.8) * mm});
            skArc(sketch, "E142.MirrorCS", {"start": v(45.95, 46.8) * mm, "mid": v(45.46, 47) * mm, "end": v(45.25, 47.5) * mm});
            skLineSegment(sketch, "E143.MirrorCS", {"start": v(45.25, 48.3) * mm, "end": v(45.25, 47.5) * mm});
            skLineSegment(sketch, "E144", {"start": v(0, 25) * mm, "end": v(-7.52, 25) * mm, "construction": true});
            skArc(sketch, "E145.MirrorCS", {"start": v(1.95, 1) * mm, "mid": v(1.46, 1.2) * mm, "end": v(1.25, 1.7) * mm});
            skLineSegment(sketch, "E146.MirrorCS", {"start": v(1.95, 1) * mm, "end": v(2.05, 1) * mm});
            skArc(sketch, "E147.MirrorCS", {"start": v(2.75, 1.7) * mm, "mid": v(2.54, 1.2) * mm, "end": v(2.05, 1) * mm});
            skLineSegment(sketch, "E148.MirrorCS", {"start": v(2.75, 1.7) * mm, "end": v(2.75, 2.5) * mm});
            skArc(sketch, "E149.MirrorCS", {"start": v(2.05, 3.2) * mm, "mid": v(2.54, 3) * mm, "end": v(2.75, 2.5) * mm});
            skLineSegment(sketch, "E150.MirrorCS", {"start": v(1.95, 3.2) * mm, "end": v(2.05, 3.2) * mm});
            skArc(sketch, "E151.MirrorCS", {"start": v(1.25, 2.5) * mm, "mid": v(1.46, 3) * mm, "end": v(1.95, 3.2) * mm});
            skLineSegment(sketch, "E152.MirrorCS", {"start": v(1.25, 1.7) * mm, "end": v(1.25, 2.5) * mm});
            skLineSegment(sketch, "E153.MirrorCS", {"start": v(46.75, 1.7) * mm, "end": v(46.75, 2.5) * mm});
            skArc(sketch, "E154.MirrorCS", {"start": v(46.05, 1) * mm, "mid": v(46.54, 1.2) * mm, "end": v(46.75, 1.7) * mm});
            skLineSegment(sketch, "E155.MirrorCS", {"start": v(46.05, 1) * mm, "end": v(45.95, 1) * mm});
            skArc(sketch, "E156.MirrorCS", {"start": v(45.25, 1.7) * mm, "mid": v(45.46, 1.2) * mm, "end": v(45.95, 1) * mm});
            skLineSegment(sketch, "E157.MirrorCS", {"start": v(45.25, 1.7) * mm, "end": v(45.25, 2.5) * mm});
            skArc(sketch, "E158.MirrorCS", {"start": v(45.95, 3.2) * mm, "mid": v(45.46, 3) * mm, "end": v(45.25, 2.5) * mm});
            skLineSegment(sketch, "E159.MirrorCS", {"start": v(46.05, 3.2) * mm, "end": v(45.95, 3.2) * mm});
            skArc(sketch, "E160.MirrorCS", {"start": v(46.75, 2.5) * mm, "mid": v(46.54, 3) * mm, "end": v(46.05, 3.2) * mm});
            skSolve(sketch);
        }
        {
            var Q0;
            Q0 = qSketchRegion(id + "F10", true);
            extrude(context, id + "F11", {"entities" : qUnion([Q0]), "operationType" : NewBodyOperationType.REMOVE, "oppositeDirection" : true, "depth" : 3 * mm});
        }
        {
            var Q0;
            Q0=makeQuery(id+"F7.boolean.opBoolean","MERGE",FACE,{"derivedFrom":[makeQuery(id+"F5.boolean.opBoolean","MERGE",FACE,{"derivedFrom":[makeQuery(id+"F3.boolean.opBoolean","MERGE",FACE,{"derivedFrom":[makeQuery(id+"F1.opExtrude","SWEPT_FACE",FACE,{"disambiguationData":[OSD([sQuery(id+"F0.wireOp",EDGE,"E0.top")])]}),makeQuery(id+"F3.opExtrude","SWEPT_FACE",FACE,{"disambiguationData":[OSD([sQuery(id+"F2.wireOp",EDGE,"E1.bottom")])]}),makeQuery(id+"F3.opExtrude","SWEPT_FACE",FACE,{"disambiguationData":[OSD([sQuery(id+"F2.wireOp",EDGE,"E3.bottom")])]})]}),makeQuery(id+"F5.opExtrude","SWEPT_FACE",FACE,{"disambiguationData":[OSD([sQuery(id+"F4.wireOp",EDGE,"E90.top")])]})]}),makeQuery(id+"F7.opExtrude","SWEPT_FACE",FACE,{"disambiguationData":[OSD([sQuery(id+"F6.wireOp",EDGE,"E91.bottom")])]}),makeQuery(id+"F7.opExtrude","SWEPT_FACE",FACE,{"disambiguationData":[OSD([sQuery(id+"F6.wireOp",EDGE,"E93.bottom")])]})]});
            var sketch = newSketch(context, id + "F12", { "sketchPlane" : qUnion([Q0])});
            skLineSegment(sketch, "E161", {"start": v(-118, 50) * mm, "end": v(-118, 49) * mm, "construction": true});
            skLineSegment(sketch, "E162", {"start": v(-118, 49) * mm, "end": v(-118.05, 49) * mm, "construction": true});
            skLineSegment(sketch, "E163.bottom", {"start": v(-118.05, 49) * mm, "end": v(-117.95, 49) * mm});
            skLineSegment(sketch, "E163.top", {"start": v(-118.05, 46.8) * mm, "end": v(-117.95, 46.8) * mm});
            skLineSegment(sketch, "E163.left", {"start": v(-118.75, 48.3) * mm, "end": v(-118.75, 47.5) * mm});
            skLineSegment(sketch, "E163.right", {"start": v(-117.25, 48.3) * mm, "end": v(-117.25, 47.5) * mm});
            skPoint(sketch, "E164.visualSharp", {"position": v(-118.75, 49) * mm});
            skArc(sketch, "E164.filletArc", {"start": v(-118.05, 49) * mm, "mid": v(-118.54, 48.8) * mm, "end": v(-118.75, 48.3) * mm});
            skPoint(sketch, "E165.visualSharp", {"position": v(-117.25, 49) * mm});
            skArc(sketch, "E165.filletArc", {"start": v(-117.25, 48.3) * mm, "mid": v(-117.46, 48.8) * mm, "end": v(-117.95, 49) * mm});
            skPoint(sketch, "E166.visualSharp", {"position": v(-117.25, 46.8) * mm});
            skArc(sketch, "E166.filletArc", {"start": v(-117.95, 46.8) * mm, "mid": v(-117.46, 47) * mm, "end": v(-117.25, 47.5) * mm});
            skPoint(sketch, "E167.visualSharp", {"position": v(-118.75, 46.8) * mm});
            skArc(sketch, "E167.filletArc", {"start": v(-118.75, 47.5) * mm, "mid": v(-118.54, 47) * mm, "end": v(-118.05, 46.8) * mm});
            skLineSegment(sketch, "E168", {"start": v(-120, 25) * mm, "end": v(-129.13, 25) * mm, "construction": true});
            skArc(sketch, "E169.MirrorCS", {"start": v(-118.05, 1) * mm, "mid": v(-118.54, 1.2) * mm, "end": v(-118.75, 1.7) * mm});
            skLineSegment(sketch, "E170.MirrorCS", {"start": v(-118.75, 1.7) * mm, "end": v(-118.75, 2.5) * mm});
            skArc(sketch, "E171.MirrorCS", {"start": v(-118.75, 2.5) * mm, "mid": v(-118.54, 3) * mm, "end": v(-118.05, 3.2) * mm});
            skLineSegment(sketch, "E172.MirrorCS", {"start": v(-118.05, 3.2) * mm, "end": v(-117.95, 3.2) * mm});
            skArc(sketch, "E173.MirrorCS", {"start": v(-117.95, 3.2) * mm, "mid": v(-117.46, 3) * mm, "end": v(-117.25, 2.5) * mm});
            skLineSegment(sketch, "E174.MirrorCS", {"start": v(-117.25, 1.7) * mm, "end": v(-117.25, 2.5) * mm});
            skArc(sketch, "E175.MirrorCS", {"start": v(-117.25, 1.7) * mm, "mid": v(-117.46, 1.2) * mm, "end": v(-117.95, 1) * mm});
            skLineSegment(sketch, "E176.MirrorCS", {"start": v(-118.05, 1) * mm, "end": v(-117.95, 1) * mm});
            skLineSegment(sketch, "E177", {"start": v(-60, 48) * mm, "end": v(-60, 55.4) * mm, "construction": true});
            skLineSegment(sketch, "E178.MirrorCS", {"start": v(-1.95, 49) * mm, "end": v(-2.05, 49) * mm});
            skArc(sketch, "E179.MirrorCS", {"start": v(-1.95, 49) * mm, "mid": v(-1.46, 48.8) * mm, "end": v(-1.25, 48.3) * mm});
            skLineSegment(sketch, "E180.MirrorCS", {"start": v(-1.25, 48.3) * mm, "end": v(-1.25, 47.5) * mm});
            skArc(sketch, "E181.MirrorCS", {"start": v(-1.25, 47.5) * mm, "mid": v(-1.46, 47) * mm, "end": v(-1.95, 46.8) * mm});
            skLineSegment(sketch, "E182.MirrorCS", {"start": v(-1.95, 46.8) * mm, "end": v(-2.05, 46.8) * mm});
            skArc(sketch, "E183.MirrorCS", {"start": v(-2.05, 46.8) * mm, "mid": v(-2.54, 47) * mm, "end": v(-2.75, 47.5) * mm});
            skLineSegment(sketch, "E184.MirrorCS", {"start": v(-2.75, 48.3) * mm, "end": v(-2.75, 47.5) * mm});
            skArc(sketch, "E185.MirrorCS", {"start": v(-2.75, 48.3) * mm, "mid": v(-2.54, 48.8) * mm, "end": v(-2.05, 49) * mm});
            skArc(sketch, "E186.MirrorCS", {"start": v(-2.75, 1.7) * mm, "mid": v(-2.54, 1.2) * mm, "end": v(-2.05, 1) * mm});
            skLineSegment(sketch, "E187.MirrorCS", {"start": v(-1.95, 1) * mm, "end": v(-2.05, 1) * mm});
            skArc(sketch, "E188.MirrorCS", {"start": v(-1.95, 1) * mm, "mid": v(-1.46, 1.2) * mm, "end": v(-1.25, 1.7) * mm});
            skLineSegment(sketch, "E189.MirrorCS", {"start": v(-2.75, 1.7) * mm, "end": v(-2.75, 2.5) * mm});
            skLineSegment(sketch, "E190.MirrorCS", {"start": v(-1.25, 1.7) * mm, "end": v(-1.25, 2.5) * mm});
            skArc(sketch, "E191.MirrorCS", {"start": v(-1.25, 2.5) * mm, "mid": v(-1.46, 3) * mm, "end": v(-1.95, 3.2) * mm});
            skLineSegment(sketch, "E192.MirrorCS", {"start": v(-1.95, 3.2) * mm, "end": v(-2.05, 3.2) * mm});
            skArc(sketch, "E193.MirrorCS", {"start": v(-2.05, 3.2) * mm, "mid": v(-2.54, 3) * mm, "end": v(-2.75, 2.5) * mm});
            skSolve(sketch);
        }
        {
            var Q0;
            Q0 = qSketchRegion(id + "F12", true);
            extrude(context, id + "F13", {"entities" : qUnion([Q0]), "operationType" : NewBodyOperationType.REMOVE, "oppositeDirection" : true, "depth" : 3 * mm});
        }
        {
            var Q0;
            Q0=makeQuery(id+"F7.boolean.opBoolean","MERGE",FACE,{"derivedFrom":[makeQuery(id+"F5.boolean.opBoolean","MERGE",FACE,{"derivedFrom":[makeQuery(id+"F3.boolean.opBoolean","MERGE",FACE,{"derivedFrom":[makeQuery(id+"F1.opExtrude","SWEPT_FACE",FACE,{"disambiguationData":[OSD([sQuery(id+"F0.wireOp",EDGE,"E0.left")])]}),makeQuery(id+"F3.opExtrude","SWEPT_FACE",FACE,{"disambiguationData":[OSD([sQuery(id+"F2.wireOp",EDGE,"E3.left")])]}),makeQuery(id+"F3.opExtrude","SWEPT_FACE",FACE,{"disambiguationData":[OSD([sQuery(id+"F2.wireOp",EDGE,"E4.left")])]})]}),makeQuery(id+"F5.opExtrude","SWEPT_FACE",FACE,{"disambiguationData":[OSD([sQuery(id+"F4.wireOp",EDGE,"E90.left")])]})]}),makeQuery(id+"F7.opExtrude","SWEPT_FACE",FACE,{"disambiguationData":[OSD([sQuery(id+"F6.wireOp",EDGE,"E91.left")])]}),makeQuery(id+"F7.opExtrude","SWEPT_FACE",FACE,{"disambiguationData":[OSD([sQuery(id+"F6.wireOp",EDGE,"E92.left")])]})]});
            var sketch = newSketch(context, id + "F14", { "sketchPlane" : qUnion([Q0])});
            skLineSegment(sketch, "E194", {"start": v(-46, 50) * mm, "end": v(-46, 49) * mm, "construction": true});
            skLineSegment(sketch, "E195", {"start": v(-46, 49) * mm, "end": v(-46.75, 49) * mm, "construction": true});
            skLineSegment(sketch, "E196.bottom", {"start": v(-46.05, 49) * mm, "end": v(-45.95, 49) * mm});
            skLineSegment(sketch, "E196.top", {"start": v(-46.05, 46.8) * mm, "end": v(-45.95, 46.8) * mm});
            skLineSegment(sketch, "E196.left", {"start": v(-46.75, 48.3) * mm, "end": v(-46.75, 47.5) * mm});
            skLineSegment(sketch, "E196.right", {"start": v(-45.25, 48.3) * mm, "end": v(-45.25, 47.5) * mm});
            skPoint(sketch, "E197.visualSharp", {"position": v(-46.75, 49) * mm});
            skArc(sketch, "E197.filletArc", {"start": v(-46.05, 49) * mm, "mid": v(-46.54, 48.8) * mm, "end": v(-46.75, 48.3) * mm});
            skPoint(sketch, "E198.visualSharp", {"position": v(-45.25, 49) * mm});
            skArc(sketch, "E198.filletArc", {"start": v(-45.25, 48.3) * mm, "mid": v(-45.46, 48.8) * mm, "end": v(-45.95, 49) * mm});
            skPoint(sketch, "E199.visualSharp", {"position": v(-45.25, 46.8) * mm});
            skArc(sketch, "E199.filletArc", {"start": v(-45.95, 46.8) * mm, "mid": v(-45.46, 47) * mm, "end": v(-45.25, 47.5) * mm});
            skPoint(sketch, "E200.visualSharp", {"position": v(-46.75, 46.8) * mm});
            skArc(sketch, "E200.filletArc", {"start": v(-46.75, 47.5) * mm, "mid": v(-46.54, 47) * mm, "end": v(-46.05, 46.8) * mm});
            skLineSegment(sketch, "E201", {"start": v(-48, 25) * mm, "end": v(-57.93, 25) * mm, "construction": true});
            skArc(sketch, "E202.MirrorCS", {"start": v(-46.75, 2.5) * mm, "mid": v(-46.54, 3) * mm, "end": v(-46.05, 3.2) * mm});
            skLineSegment(sketch, "E203.MirrorCS", {"start": v(-46.05, 3.2) * mm, "end": v(-45.95, 3.2) * mm});
            skArc(sketch, "E204.MirrorCS", {"start": v(-45.95, 3.2) * mm, "mid": v(-45.46, 3) * mm, "end": v(-45.25, 2.5) * mm});
            skLineSegment(sketch, "E205.MirrorCS", {"start": v(-45.25, 1.7) * mm, "end": v(-45.25, 2.5) * mm});
            skArc(sketch, "E206.MirrorCS", {"start": v(-45.25, 1.7) * mm, "mid": v(-45.46, 1.2) * mm, "end": v(-45.95, 1) * mm});
            skLineSegment(sketch, "E207.MirrorCS", {"start": v(-46.05, 1) * mm, "end": v(-45.95, 1) * mm});
            skArc(sketch, "E208.MirrorCS", {"start": v(-46.05, 1) * mm, "mid": v(-46.54, 1.2) * mm, "end": v(-46.75, 1.7) * mm});
            skLineSegment(sketch, "E209.MirrorCS", {"start": v(-46.75, 1.7) * mm, "end": v(-46.75, 2.5) * mm});
            skLineSegment(sketch, "E210", {"start": v(-24, 48) * mm, "end": v(-24, 53.33) * mm, "construction": true});
            skArc(sketch, "E211.MirrorCS", {"start": v(-2.75, 48.3) * mm, "mid": v(-2.54, 48.8) * mm, "end": v(-2.05, 49) * mm});
            skLineSegment(sketch, "E212.MirrorCS", {"start": v(-1.95, 49) * mm, "end": v(-2.05, 49) * mm});
            skArc(sketch, "E213.MirrorCS", {"start": v(-1.95, 49) * mm, "mid": v(-1.46, 48.8) * mm, "end": v(-1.25, 48.3) * mm});
            skLineSegment(sketch, "E214.MirrorCS", {"start": v(-1.25, 48.3) * mm, "end": v(-1.25, 47.5) * mm});
            skArc(sketch, "E215.MirrorCS", {"start": v(-1.25, 47.5) * mm, "mid": v(-1.46, 47) * mm, "end": v(-1.95, 46.8) * mm});
            skLineSegment(sketch, "E216.MirrorCS", {"start": v(-1.95, 46.8) * mm, "end": v(-2.05, 46.8) * mm});
            skArc(sketch, "E217.MirrorCS", {"start": v(-2.05, 46.8) * mm, "mid": v(-2.54, 47) * mm, "end": v(-2.75, 47.5) * mm});
            skLineSegment(sketch, "E218.MirrorCS", {"start": v(-2.75, 48.3) * mm, "end": v(-2.75, 47.5) * mm});
            skArc(sketch, "E219.MirrorCS", {"start": v(-1.95, 1) * mm, "mid": v(-1.46, 1.2) * mm, "end": v(-1.25, 1.7) * mm});
            skLineSegment(sketch, "E220.MirrorCS", {"start": v(-1.95, 1) * mm, "end": v(-2.05, 1) * mm});
            skArc(sketch, "E221.MirrorCS", {"start": v(-2.75, 1.7) * mm, "mid": v(-2.54, 1.2) * mm, "end": v(-2.05, 1) * mm});
            skLineSegment(sketch, "E222.MirrorCS", {"start": v(-2.75, 1.7) * mm, "end": v(-2.75, 2.5) * mm});
            skLineSegment(sketch, "E223.MirrorCS", {"start": v(-1.95, 3.2) * mm, "end": v(-2.05, 3.2) * mm});
            skArc(sketch, "E224.MirrorCS", {"start": v(-1.25, 2.5) * mm, "mid": v(-1.46, 3) * mm, "end": v(-1.95, 3.2) * mm});
            skLineSegment(sketch, "E225.MirrorCS", {"start": v(-1.25, 1.7) * mm, "end": v(-1.25, 2.5) * mm});
            skArc(sketch, "E226.MirrorCS", {"start": v(-2.05, 3.2) * mm, "mid": v(-2.54, 3) * mm, "end": v(-2.75, 2.5) * mm});
            skSolve(sketch);
        }
        {
            var Q0;
            Q0 = qSketchRegion(id + "F14", true);
            extrude(context, id + "F15", {"entities" : qUnion([Q0]), "operationType" : NewBodyOperationType.REMOVE, "oppositeDirection" : true, "depth" : 3 * mm});
        }
        {
            var Q0;
            Q0=makeQuery(id+"F3.opExtrude","SWEPT_FACE",FACE,{"disambiguationData":[OSD([sQuery(id+"F2.wireOp",EDGE,"E72")])]});
            var sketch = newSketch(context, id + "F16", { "sketchPlane" : qUnion([Q0])});
            skLineSegment(sketch, "E227.bottom", {"start": v(-6.05, 5) * mm, "end": v(-26.05, 5) * mm});
            skLineSegment(sketch, "E227.top", {"start": v(-6.05, 40) * mm, "end": v(-26.05, 40) * mm});
            skLineSegment(sketch, "E227.left", {"start": v(-6.05, 5) * mm, "end": v(-6.05, 40) * mm});
            skLineSegment(sketch, "E227.right", {"start": v(-26.05, 5) * mm, "end": v(-26.05, 40) * mm});
            skSolve(sketch);
        }
        {
            var Q0;
            Q0 = qSketchRegion(id + "F16", true);
            extrude(context, id + "F17", {"entities" : qUnion([Q0]), "operationType" : NewBodyOperationType.ADD, "oppositeDirection" : true, "depth" : 2 * mm, "hasSecondDirection" : true, "secondDirectionOppositeDirection" : false, "secondDirectionDepth" : 1 * mm});
        }
        {
            var Q0;
            Q0=makeQuery(id+"F17.opExtrude","CAP_FACE",FACE,{"disambiguationData":[OSD([sQuery(id+"F16.wireOp",EDGE,"E227.bottom"),sQuery(id+"F16.wireOp",EDGE,"E227.top"),sQuery(id+"F16.wireOp",EDGE,"E227.left"),sQuery(id+"F16.wireOp",EDGE,"E227.right")])],"isStart":true});
            var sketch = newSketch(context, id + "F18", { "sketchPlane" : qUnion([Q0])});
            skLineSegment(sketch, "E228", {"start": v(-6.05, 5) * mm, "end": v(-7.05, 5) * mm, "construction": true});
            skLineSegment(sketch, "E229", {"start": v(-7.05, 5) * mm, "end": v(-7.05, 5.5) * mm, "construction": true});
            skLineSegment(sketch, "E230.bottom", {"start": v(-7.05, 5.5) * mm, "end": v(-25.05, 5.5) * mm});
            skLineSegment(sketch, "E230.top", {"start": v(-7.05, 39.5) * mm, "end": v(-25.05, 39.5) * mm});
            skLineSegment(sketch, "E230.left", {"start": v(-7.05, 5.5) * mm, "end": v(-7.05, 39.5) * mm});
            skLineSegment(sketch, "E230.right", {"start": v(-25.05, 5.5) * mm, "end": v(-25.05, 39.5) * mm});
            skSolve(sketch);
        }
        {
            var Q0;
            Q0 = qSketchRegion(id + "F18", true);
            extrude(context, id + "F19", {"entities" : qUnion([Q0]), "operationType" : NewBodyOperationType.REMOVE, "oppositeDirection" : true, "depth" : 0.5 * mm});
        }
        {
            var Q0;
            Q0=makeQuery(id+"F7.boolean.opBoolean","MERGE",FACE,{"derivedFrom":[makeQuery(id+"F5.boolean.opBoolean","MERGE",FACE,{"derivedFrom":[makeQuery(id+"F3.boolean.opBoolean","MERGE",FACE,{"derivedFrom":[makeQuery(id+"F1.opExtrude","SWEPT_FACE",FACE,{"disambiguationData":[OSD([sQuery(id+"F0.wireOp",EDGE,"E0.right")])]}),makeQuery(id+"F3.opExtrude","SWEPT_FACE",FACE,{"disambiguationData":[OSD([sQuery(id+"F2.wireOp",EDGE,"E1.left")])]}),makeQuery(id+"F3.opExtrude","SWEPT_FACE",FACE,{"disambiguationData":[OSD([sQuery(id+"F2.wireOp",EDGE,"E2.left")])]})]}),makeQuery(id+"F5.opExtrude","SWEPT_FACE",FACE,{"disambiguationData":[OSD([sQuery(id+"F4.wireOp",EDGE,"E90.right")])]})]}),makeQuery(id+"F7.opExtrude","SWEPT_FACE",FACE,{"disambiguationData":[OSD([sQuery(id+"F6.wireOp",EDGE,"E93.left")])]}),makeQuery(id+"F7.opExtrude","SWEPT_FACE",FACE,{"disambiguationData":[OSD([sQuery(id+"F6.wireOp",EDGE,"E94.left")])]})]});
            var sketch = newSketch(context, id + "F20", { "sketchPlane" : qUnion([Q0])});
            skLineSegment(sketch, "E231", {"start": v(0, 25) * mm, "end": v(48, 25) * mm, "construction": true});
            skLineSegment(sketch, "E232", {"start": v(24, 0) * mm, "end": v(24, 48) * mm, "construction": true});
            skLineSegment(sketch, "E233", {"start": v(7, 25) * mm, "end": v(7, 37) * mm});
            skLineSegment(sketch, "E234", {"start": v(7, 37) * mm, "end": v(19, 37) * mm});
            skLineSegment(sketch, "E235", {"start": v(19, 37) * mm, "end": v(19, 25) * mm});
            skLineSegment(sketch, "E236", {"start": v(19, 25) * mm, "end": v(7, 25) * mm});
            skLineSegment(sketch, "E237.MirrorCS", {"start": v(41, 37) * mm, "end": v(29, 37) * mm});
            skLineSegment(sketch, "E238.MirrorCS", {"start": v(29, 37) * mm, "end": v(29, 25) * mm});
            skLineSegment(sketch, "E239.MirrorCS", {"start": v(41, 25) * mm, "end": v(41, 37) * mm});
            skLineSegment(sketch, "E240", {"start": v(29, 25) * mm, "end": v(41, 25) * mm});
            skSolve(sketch);
        }
        {
            var Q0;
            Q0 = qSketchRegion(id + "F20", true);
            extrude(context, id + "F21", {"entities" : qUnion([Q0]), "operationType" : NewBodyOperationType.ADD, "oppositeDirection" : true, "depth" : 2 * mm});
        }
        {
            var Q0;
            Q0=makeQuery(id+"F21.opExtrude","CAP_FACE",FACE,{"disambiguationData":[OSD([sQuery(id+"F20.wireOp",EDGE,"E233"),sQuery(id+"F20.wireOp",EDGE,"E234"),sQuery(id+"F20.wireOp",EDGE,"E235"),sQuery(id+"F20.wireOp",EDGE,"E236")])],"isStart":true});
            var sketch = newSketch(context, id + "F22", { "sketchPlane" : qUnion([Q0])});
            skLineSegment(sketch, "E241", {"start": v(7, 37) * mm, "end": v(8, 37) * mm, "construction": true});
            skLineSegment(sketch, "E242", {"start": v(8, 37) * mm, "end": v(8, 36) * mm, "construction": true});
            skLineSegment(sketch, "E243.bottom", {"start": v(8, 36) * mm, "end": v(18, 36) * mm});
            skLineSegment(sketch, "E243.top", {"start": v(8, 26) * mm, "end": v(18, 26) * mm});
            skLineSegment(sketch, "E243.left", {"start": v(8, 36) * mm, "end": v(8, 26) * mm});
            skLineSegment(sketch, "E243.right", {"start": v(18, 36) * mm, "end": v(18, 26) * mm});
            skSolve(sketch);
        }
        {
            var Q0;
            Q0 = qSketchRegion(id + "F22", true);
            extrude(context, id + "F23", {"entities" : qUnion([Q0]), "operationType" : NewBodyOperationType.REMOVE, "oppositeDirection" : true, "depth" : 25 * mm});
        }
        {
            var Q0;
            Q0=makeQuery(id+"F21.opExtrude","CAP_FACE",FACE,{"disambiguationData":[OSD([sQuery(id+"F20.wireOp",EDGE,"E237.MirrorCS"),sQuery(id+"F20.wireOp",EDGE,"E238.MirrorCS"),sQuery(id+"F20.wireOp",EDGE,"E239.MirrorCS"),sQuery(id+"F20.wireOp",EDGE,"E240")])],"isStart":true});
            var sketch = newSketch(context, id + "F24", { "sketchPlane" : qUnion([Q0])});
            skLineSegment(sketch, "E244", {"start": v(29, 37) * mm, "end": v(30, 37) * mm, "construction": true});
            skLineSegment(sketch, "E245", {"start": v(30, 37) * mm, "end": v(30, 36) * mm, "construction": true});
            skLineSegment(sketch, "E246.bottom", {"start": v(30, 36) * mm, "end": v(40, 36) * mm});
            skLineSegment(sketch, "E246.top", {"start": v(30, 26) * mm, "end": v(40, 26) * mm});
            skLineSegment(sketch, "E246.left", {"start": v(30, 36) * mm, "end": v(30, 26) * mm});
            skLineSegment(sketch, "E246.right", {"start": v(40, 36) * mm, "end": v(40, 26) * mm});
            skSolve(sketch);
        }
        {
            var Q0;
            Q0=makeQuery(id+"F24.imprint","IMPRINT",FACE,{"disambiguationData":[TD([[makeQuery(id+"F24.imprint","IMPRINT",EDGE,{"derivedFrom":sQuery(id+"F24.wireOp",EDGE,"E246.bottom")}),-1.0]])]});
            extrude(context, id + "F25", {"entities" : qUnion([Q0]), "operationType" : NewBodyOperationType.REMOVE, "oppositeDirection" : true, "depth" : 25 * mm});
        }
        {
            var Q0;
            Q0=makeQuery(id+"F7.boolean.opBoolean","MERGE",FACE,{"derivedFrom":[makeQuery(id+"F5.boolean.opBoolean","MERGE",FACE,{"derivedFrom":[makeQuery(id+"F3.boolean.opBoolean","MERGE",FACE,{"derivedFrom":[makeQuery(id+"F1.opExtrude","SWEPT_FACE",FACE,{"disambiguationData":[OSD([sQuery(id+"F0.wireOp",EDGE,"E0.top")])]}),makeQuery(id+"F3.opExtrude","SWEPT_FACE",FACE,{"disambiguationData":[OSD([sQuery(id+"F2.wireOp",EDGE,"E1.bottom")])]}),makeQuery(id+"F3.opExtrude","SWEPT_FACE",FACE,{"disambiguationData":[OSD([sQuery(id+"F2.wireOp",EDGE,"E3.bottom")])]})]}),makeQuery(id+"F5.opExtrude","SWEPT_FACE",FACE,{"disambiguationData":[OSD([sQuery(id+"F4.wireOp",EDGE,"E90.top")])]})]}),makeQuery(id+"F7.opExtrude","SWEPT_FACE",FACE,{"disambiguationData":[OSD([sQuery(id+"F6.wireOp",EDGE,"E91.bottom")])]}),makeQuery(id+"F7.opExtrude","SWEPT_FACE",FACE,{"disambiguationData":[OSD([sQuery(id+"F6.wireOp",EDGE,"E93.bottom")])]})]});
            var sketch = newSketch(context, id + "F26", { "sketchPlane" : qUnion([Q0])});
            skLineSegment(sketch, "E247", {"start": v(-60, 0) * mm, "end": v(-60, 5) * mm, "construction": true});
            skLineSegment(sketch, "E248", {"start": v(-60, 2.5) * mm, "end": v(-75, 2.5) * mm, "construction": true});
            skLineSegment(sketch, "E249", {"start": v(-75, 2.5) * mm, "end": v(-75, 3.5) * mm, "construction": true});
            skLineSegment(sketch, "E250.bottom", {"start": v(-75, 3.5) * mm, "end": v(-85, 3.5) * mm});
            skLineSegment(sketch, "E250.top", {"start": v(-75, 1.5) * mm, "end": v(-85, 1.5) * mm});
            skLineSegment(sketch, "E250.left", {"start": v(-75, 3.5) * mm, "end": v(-75, 1.5) * mm});
            skLineSegment(sketch, "E250.right", {"start": v(-85, 3.5) * mm, "end": v(-85, 1.5) * mm});
            skLineSegment(sketch, "E251.MirrorCS", {"start": v(-45, 1.5) * mm, "end": v(-35, 1.5) * mm});
            skLineSegment(sketch, "E252.MirrorCS", {"start": v(-45, 3.5) * mm, "end": v(-45, 1.5) * mm});
            skLineSegment(sketch, "E253.MirrorCS", {"start": v(-45, 3.5) * mm, "end": v(-35, 3.5) * mm});
            skLineSegment(sketch, "E254.MirrorCS", {"start": v(-35, 3.5) * mm, "end": v(-35, 1.5) * mm});
            skSolve(sketch);
        }
        {
            var Q0;
            Q0 = qSketchRegion(id + "F26", true);
            extrude(context, id + "F27", {"entities" : qUnion([Q0]), "operationType" : NewBodyOperationType.REMOVE, "oppositeDirection" : true, "depth" : 50 * mm});
        }
        {
            var Q0;
            Q0=makeQuery(id+"F7.boolean.opBoolean","MERGE",FACE,{"derivedFrom":[makeQuery(id+"F5.boolean.opBoolean","MERGE",FACE,{"derivedFrom":[makeQuery(id+"F3.boolean.opBoolean","MERGE",FACE,{"derivedFrom":[makeQuery(id+"F1.opExtrude","SWEPT_FACE",FACE,{"disambiguationData":[OSD([sQuery(id+"F0.wireOp",EDGE,"E0.bottom")])]}),makeQuery(id+"F3.opExtrude","SWEPT_FACE",FACE,{"disambiguationData":[OSD([sQuery(id+"F2.wireOp",EDGE,"E2.bottom")])]}),makeQuery(id+"F3.opExtrude","SWEPT_FACE",FACE,{"disambiguationData":[OSD([sQuery(id+"F2.wireOp",EDGE,"E4.bottom")])]})]}),makeQuery(id+"F5.opExtrude","SWEPT_FACE",FACE,{"disambiguationData":[OSD([sQuery(id+"F4.wireOp",EDGE,"E90.bottom")])]})]}),makeQuery(id+"F7.opExtrude","SWEPT_FACE",FACE,{"disambiguationData":[OSD([sQuery(id+"F6.wireOp",EDGE,"E92.bottom")])]}),makeQuery(id+"F7.opExtrude","SWEPT_FACE",FACE,{"disambiguationData":[OSD([sQuery(id+"F6.wireOp",EDGE,"E94.bottom")])]})]});
            var sketch = newSketch(context, id + "F28", { "sketchPlane" : qUnion([Q0])});
            skLineSegment(sketch, "E255.bottom", {"start": v(0, 45) * mm, "end": v(120, 45) * mm});
            skLineSegment(sketch, "E255.top", {"start": v(0, 50) * mm, "end": v(120, 50) * mm});
            skLineSegment(sketch, "E255.left", {"start": v(0, 45) * mm, "end": v(0, 50) * mm});
            skLineSegment(sketch, "E255.right", {"start": v(120, 45) * mm, "end": v(120, 50) * mm});
            skSolve(sketch);
        }
        {
            var Q0;
            Q0 = qSketchRegion(id + "F28", true);
            extrude(context, id + "F29", {"entities" : qUnion([Q0]), "operationType" : NewBodyOperationType.REMOVE, "oppositeDirection" : true, "depth" : 50 * mm});
        }
        {
            var Q0;
            Q0=makeQuery(id+"F29.boolean.opBoolean","COPY",FACE,{"derivedFrom":makeQuery(id+"F29.opExtrude","SWEPT_FACE",FACE,{"disambiguationData":[OSD([sQuery(id+"F28.wireOp",EDGE,"E255.bottom")])]})});
            var sketch = newSketch(context, id + "F30", { "sketchPlane" : qUnion([Q0])});
            skCircle(sketch, "E256", {"center": v(2, 46) * mm, "radius": 0.5 * mm});
            skPoint(sketch, "E256.centerSnap0", {"position": v(0, 46) * mm});
            skPoint(sketch, "E256.centerSnap1", {"position": v(2, 48) * mm});
            skCircle(sketch, "E257", {"center": v(118, 46) * mm, "radius": 0.5 * mm});
            skPoint(sketch, "E257.centerSnap0", {"position": v(120, 46) * mm});
            skPoint(sketch, "E257.centerSnap1", {"position": v(118, 48) * mm});
            skCircle(sketch, "E258", {"center": v(118, 2) * mm, "radius": 0.5 * mm});
            skPoint(sketch, "E258.centerSnap0", {"position": v(120, 2) * mm});
            skPoint(sketch, "E258.centerSnap1", {"position": v(118, 0) * mm});
            skCircle(sketch, "E259", {"center": v(2, 2) * mm, "radius": 0.5 * mm});
            skPoint(sketch, "E259.centerSnap0", {"position": v(0, 2) * mm});
            skPoint(sketch, "E259.centerSnap1", {"position": v(2, 0) * mm});
            skSolve(sketch);
        }
        {
            var Q0;
            Q0 = qSketchRegion(id + "F30", true);
            extrude(context, id + "F31", {"entities" : qUnion([Q0]), "operationType" : NewBodyOperationType.ADD, "depth" : 2 * mm});
        }
        {
            var Q0;
            Q0=qCreatedBy(makeId("Top.planeOp"),FACE);
            var sketch = newSketch(context, id + "F32", { "sketchPlane" : qUnion([Q0])});
            skLineSegment(sketch, "E260", {"start": v(0, 0) * mm, "end": v(0, -10) * mm, "construction": true});
            skLineSegment(sketch, "E261.bottom", {"start": v(0, -10) * mm, "end": v(120, -10) * mm});
            skLineSegment(sketch, "E261.top", {"start": v(0, -58) * mm, "end": v(120, -58) * mm});
            skLineSegment(sketch, "E261.left", {"start": v(0, -10) * mm, "end": v(0, -58) * mm});
            skLineSegment(sketch, "E261.right", {"start": v(120, -10) * mm, "end": v(120, -58) * mm});
            skSolve(sketch);
        }
        {
            var Q0;
            Q0=makeQuery(id+"F32.imprint","IMPRINT",FACE,{"disambiguationData":[TD([[makeQuery(id+"F32.imprint","IMPRINT",EDGE,{"derivedFrom":sQuery(id+"F32.wireOp",EDGE,"E261.bottom")}),-1.0]])]});
            var Q1;
            Q1 = qConstructionFilter(qBodyType(qCreatedBy(id + "F32" ,EDGE), BodyType.WIRE), ConstructionObject.NO);
            extrude(context, id + "F33", {"entities" : qUnion([Q0]), "surfaceEntities" : qUnion([Q1]), "depth" : 4 * mm});
        }
        {
            var Q0;
            Q0=makeQuery(id+"F33.opExtrude","CAP_FACE",FACE,{"disambiguationData":[OSD([sQuery(id+"F32.wireOp",EDGE,"E261.bottom"),sQuery(id+"F32.wireOp",EDGE,"E261.top"),sQuery(id+"F32.wireOp",EDGE,"E261.left"),sQuery(id+"F32.wireOp",EDGE,"E261.right")])],"isStart":false});
            var sketch = newSketch(context, id + "F34", { "sketchPlane" : qUnion([Q0])});
            skLineSegment(sketch, "E262.bottom", {"start": v(0, -10) * mm, "end": v(4, -10) * mm});
            skLineSegment(sketch, "E262.top", {"start": v(0, -14) * mm, "end": v(4, -14) * mm});
            skLineSegment(sketch, "E262.left", {"start": v(0, -10) * mm, "end": v(0, -14) * mm});
            skLineSegment(sketch, "E262.right", {"start": v(4, -10) * mm, "end": v(4, -14) * mm});
            skLineSegment(sketch, "E263.bottom", {"start": v(120, -10) * mm, "end": v(116, -10) * mm});
            skLineSegment(sketch, "E263.top", {"start": v(120, -14) * mm, "end": v(116, -14) * mm});
            skLineSegment(sketch, "E263.left", {"start": v(120, -10) * mm, "end": v(120, -14) * mm});
            skLineSegment(sketch, "E263.right", {"start": v(116, -10) * mm, "end": v(116, -14) * mm});
            skLineSegment(sketch, "E264.bottom", {"start": v(120, -58) * mm, "end": v(116, -58) * mm});
            skLineSegment(sketch, "E264.top", {"start": v(120, -54) * mm, "end": v(116, -54) * mm});
            skLineSegment(sketch, "E264.left", {"start": v(120, -58) * mm, "end": v(120, -54) * mm});
            skLineSegment(sketch, "E264.right", {"start": v(116, -58) * mm, "end": v(116, -54) * mm});
            skLineSegment(sketch, "E265.bottom", {"start": v(0, -58) * mm, "end": v(4, -58) * mm});
            skLineSegment(sketch, "E265.top", {"start": v(0, -54) * mm, "end": v(4, -54) * mm});
            skLineSegment(sketch, "E265.left", {"start": v(0, -58) * mm, "end": v(0, -54) * mm});
            skLineSegment(sketch, "E265.right", {"start": v(4, -58) * mm, "end": v(4, -54) * mm});
            skSolve(sketch);
        }
        {
            var Q0;
            Q0 = qSketchRegion(id + "F34", true);
            extrude(context, id + "F35", {"entities" : qUnion([Q0]), "operationType" : NewBodyOperationType.ADD, "depth" : 2 * mm});
        }
        {
            var Q0;
            Q0=makeQuery(id+"F35.boolean.opBoolean","MERGE",FACE,{"derivedFrom":[makeQuery(id+"F33.opExtrude","SWEPT_FACE",FACE,{"disambiguationData":[OSD([sQuery(id+"F32.wireOp",EDGE,"E261.top")])]}),makeQuery(id+"F35.opExtrude","SWEPT_FACE",FACE,{"disambiguationData":[OSD([sQuery(id+"F34.wireOp",EDGE,"E264.bottom")])]}),makeQuery(id+"F35.opExtrude","SWEPT_FACE",FACE,{"disambiguationData":[OSD([sQuery(id+"F34.wireOp",EDGE,"E265.bottom")])]})]});
            var sketch = newSketch(context, id + "F36", { "sketchPlane" : qUnion([Q0])});
            skLineSegment(sketch, "E266", {"start": v(2, 6) * mm, "end": v(2, 4) * mm, "construction": true});
            skPoint(sketch, "E266.endSnap0", {"position": v(2, 6) * mm});
            skLineSegment(sketch, "E267", {"start": v(2, 4) * mm, "end": v(1.95, 4) * mm, "construction": true});
            skLineSegment(sketch, "E268.bottom", {"start": v(1.95, 4) * mm, "end": v(2.05, 4) * mm});
            skLineSegment(sketch, "E268.top", {"start": v(1.95, 1.8) * mm, "end": v(2.05, 1.8) * mm});
            skLineSegment(sketch, "E268.left", {"start": v(1.25, 3.3) * mm, "end": v(1.25, 2.5) * mm});
            skLineSegment(sketch, "E268.right", {"start": v(2.75, 3.3) * mm, "end": v(2.75, 2.5) * mm});
            skPoint(sketch, "E269.visualSharp", {"position": v(1.25, 4) * mm});
            skArc(sketch, "E269.filletArc", {"start": v(1.95, 4) * mm, "mid": v(1.46, 3.8) * mm, "end": v(1.25, 3.3) * mm});
            skPoint(sketch, "E270.visualSharp", {"position": v(2.75, 4) * mm});
            skArc(sketch, "E270.filletArc", {"start": v(2.75, 3.3) * mm, "mid": v(2.54, 3.8) * mm, "end": v(2.05, 4) * mm});
            skPoint(sketch, "E271.visualSharp", {"position": v(2.75, 1.8) * mm});
            skArc(sketch, "E271.filletArc", {"start": v(2.05, 1.8) * mm, "mid": v(2.54, 2) * mm, "end": v(2.75, 2.5) * mm});
            skPoint(sketch, "E272.visualSharp", {"position": v(1.25, 1.8) * mm});
            skArc(sketch, "E272.filletArc", {"start": v(1.25, 2.5) * mm, "mid": v(1.46, 2) * mm, "end": v(1.95, 1.8) * mm});
            skLineSegment(sketch, "E273", {"start": v(60, 0) * mm, "end": v(60, -6.23) * mm, "construction": true});
            skLineSegment(sketch, "E274.MirrorCS", {"start": v(118.75, 3.3) * mm, "end": v(118.75, 2.5) * mm});
            skArc(sketch, "E275.MirrorCS", {"start": v(118.75, 2.5) * mm, "mid": v(118.54, 2) * mm, "end": v(118.05, 1.8) * mm});
            skLineSegment(sketch, "E276.MirrorCS", {"start": v(118.05, 1.8) * mm, "end": v(117.95, 1.8) * mm});
            skArc(sketch, "E277.MirrorCS", {"start": v(117.95, 1.8) * mm, "mid": v(117.46, 2) * mm, "end": v(117.25, 2.5) * mm});
            skLineSegment(sketch, "E278.MirrorCS", {"start": v(117.25, 3.3) * mm, "end": v(117.25, 2.5) * mm});
            skArc(sketch, "E279.MirrorCS", {"start": v(117.25, 3.3) * mm, "mid": v(117.46, 3.8) * mm, "end": v(117.95, 4) * mm});
            skLineSegment(sketch, "E280.MirrorCS", {"start": v(118.05, 4) * mm, "end": v(117.95, 4) * mm});
            skArc(sketch, "E281.MirrorCS", {"start": v(118.05, 4) * mm, "mid": v(118.54, 3.8) * mm, "end": v(118.75, 3.3) * mm});
            skSolve(sketch);
        }
        {
            var Q0;
            Q0=makeQuery(id+"F33.opExtrude","CAP_FACE",FACE,{"disambiguationData":[OSD([sQuery(id+"F32.wireOp",EDGE,"E261.bottom"),sQuery(id+"F32.wireOp",EDGE,"E261.top"),sQuery(id+"F32.wireOp",EDGE,"E261.left"),sQuery(id+"F32.wireOp",EDGE,"E261.right")])],"isStart":true});
            var sketch = newSketch(context, id + "F37", { "sketchPlane" : qUnion([Q0])});
            skLineSegment(sketch, "E282", {"start": v(0, 58) * mm, "end": v(2, 58) * mm, "construction": true});
            skLineSegment(sketch, "E283", {"start": v(2, 58) * mm, "end": v(2, 56) * mm, "construction": true});
            skCircle(sketch, "E284", {"center": v(2, 56) * mm, "radius": 0.75 * mm});
            skLineSegment(sketch, "E285", {"start": v(60, 58) * mm, "end": v(60, 62.53) * mm, "construction": true});
            skPoint(sketch, "E285.endSnap0", {"position": v(60, 58) * mm});
            skCircle(sketch, "E286.MirrorC", {"center": v(118, 56) * mm, "radius": 0.75 * mm});
            skLineSegment(sketch, "E287", {"start": v(0, 34) * mm, "end": v(-4.56, 34) * mm, "construction": true});
            skPoint(sketch, "E287.endSnap0", {"position": v(0, 34) * mm});
            skCircle(sketch, "E288.MirrorC", {"center": v(2, 12) * mm, "radius": 0.75 * mm});
            skCircle(sketch, "E289.MirrorC", {"center": v(118, 12) * mm, "radius": 0.75 * mm});
            skSolve(sketch);
        }
        {
            var Q0;
            Q0 = qSketchRegion(id + "F37", true);
            extrude(context, id + "F38", {"entities" : qUnion([Q0]), "operationType" : NewBodyOperationType.REMOVE, "oppositeDirection" : true, "depth" : 2 * mm});
        }
        {
            var Q0;
            Q0 = qSketchRegion(id + "F36", true);
            extrude(context, id + "F39", {"entities" : qUnion([Q0]), "operationType" : NewBodyOperationType.REMOVE, "oppositeDirection" : true, "depth" : 48 * mm});
        }
        {
            var Q0;
            Q0=makeQuery(id+"F35.boolean.opBoolean","MERGE",FACE,{"derivedFrom":[makeQuery(id+"F33.opExtrude","SWEPT_FACE",FACE,{"disambiguationData":[OSD([sQuery(id+"F32.wireOp",EDGE,"E261.left")])]}),makeQuery(id+"F35.opExtrude","SWEPT_FACE",FACE,{"disambiguationData":[OSD([sQuery(id+"F34.wireOp",EDGE,"E262.left")])]}),makeQuery(id+"F35.opExtrude","SWEPT_FACE",FACE,{"disambiguationData":[OSD([sQuery(id+"F34.wireOp",EDGE,"E265.left")])]})]});
            var sketch = newSketch(context, id + "F40", { "sketchPlane" : qUnion([Q0])});
            skLineSegment(sketch, "E290", {"start": v(12, 6) * mm, "end": v(12, 4) * mm, "construction": true});
            skPoint(sketch, "E290.endSnap0", {"position": v(12, 6) * mm});
            skLineSegment(sketch, "E291", {"start": v(12, 4) * mm, "end": v(11.95, 4) * mm});
            skLineSegment(sketch, "E292", {"start": v(11.25, 3.3) * mm, "end": v(11.25, 2.5) * mm});
            skLineSegment(sketch, "E293", {"start": v(11.95, 1.8) * mm, "end": v(12.05, 1.8) * mm});
            skLineSegment(sketch, "E294", {"start": v(12.75, 2.5) * mm, "end": v(12.75, 3.3) * mm});
            skLineSegment(sketch, "E295", {"start": v(12.05, 4) * mm, "end": v(12, 4) * mm});
            skPoint(sketch, "E296.visualSharp", {"position": v(11.25, 4) * mm});
            skArc(sketch, "E296.filletArc", {"start": v(11.95, 4) * mm, "mid": v(11.46, 3.8) * mm, "end": v(11.25, 3.3) * mm});
            skPoint(sketch, "E297.visualSharp", {"position": v(12.75, 4) * mm});
            skArc(sketch, "E297.filletArc", {"start": v(12.75, 3.3) * mm, "mid": v(12.54, 3.8) * mm, "end": v(12.05, 4) * mm});
            skPoint(sketch, "E298.visualSharp", {"position": v(12.75, 1.8) * mm});
            skArc(sketch, "E298.filletArc", {"start": v(12.05, 1.8) * mm, "mid": v(12.54, 2) * mm, "end": v(12.75, 2.5) * mm});
            skPoint(sketch, "E299.visualSharp", {"position": v(11.25, 1.8) * mm});
            skArc(sketch, "E299.filletArc", {"start": v(11.25, 2.5) * mm, "mid": v(11.46, 2) * mm, "end": v(11.95, 1.8) * mm});
            skLineSegment(sketch, "E300", {"start": v(34, 0) * mm, "end": v(34, -2.68) * mm, "construction": true});
            skArc(sketch, "E301.MirrorCS", {"start": v(56.05, 4) * mm, "mid": v(56.54, 3.8) * mm, "end": v(56.75, 3.3) * mm});
            skLineSegment(sketch, "E302.MirrorCS", {"start": v(56, 4) * mm, "end": v(56.05, 4) * mm});
            skLineSegment(sketch, "E303.MirrorCS", {"start": v(55.95, 4) * mm, "end": v(56, 4) * mm});
            skArc(sketch, "E304.MirrorCS", {"start": v(55.25, 3.3) * mm, "mid": v(55.46, 3.8) * mm, "end": v(55.95, 4) * mm});
            skLineSegment(sketch, "E305.MirrorCS", {"start": v(55.25, 2.5) * mm, "end": v(55.25, 3.3) * mm});
            skLineSegment(sketch, "E306.MirrorCS", {"start": v(56.05, 1.8) * mm, "end": v(55.95, 1.8) * mm});
            skArc(sketch, "E307.MirrorCS", {"start": v(56.75, 2.5) * mm, "mid": v(56.54, 2) * mm, "end": v(56.05, 1.8) * mm});
            skLineSegment(sketch, "E308.MirrorCS", {"start": v(56.75, 3.3) * mm, "end": v(56.75, 2.5) * mm});
            skArc(sketch, "E309.MirrorCS", {"start": v(55.95, 1.8) * mm, "mid": v(55.46, 2) * mm, "end": v(55.25, 2.5) * mm});
            skSolve(sketch);
        }
        {
            var Q0;
            Q0 = qSketchRegion(id + "F40", true);
            extrude(context, id + "F41", {"entities" : qUnion([Q0]), "operationType" : NewBodyOperationType.REMOVE, "oppositeDirection" : true, "depth" : 120 * mm});
        }
        {
            var Q0;
            {var subQ6=makeQuery(id+"F35.opExtrude","SWEPT_FACE",FACE,{"disambiguationData":[OSD([sQuery(id+"F34.wireOp",EDGE,"E262.top")])]});var subQ8=sQuery(id+"F32.wireOp",EDGE,"E261.top");var subQ9=sQuery(id+"F32.wireOp",EDGE,"E261.bottom");var subQ10=makeQuery(id+"F33.opExtrude","CAP_FACE",FACE,{"disambiguationData":[OSD([subQ9,subQ8,sQuery(id+"F32.wireOp",EDGE,"E261.left"),sQuery(id+"F32.wireOp",EDGE,"E261.right")])],"isStart":false});var subQ21=makeQuery(id+"F33.opExtrude","SWEPT_FACE",FACE,{"disambiguationData":[OSD([subQ9])]});Q0=makeQuery(id+"F41.boolean.opBoolean","SPLIT",FACE,{"disambiguationData":[TD([subQ6])],"derivedFrom":makeQuery(id+"F39.boolean.opBoolean","SPLIT",FACE,{"disambiguationData":[TD([subQ21])],"derivedFrom":subQ10})});}
            var sketch = newSketch(context, id + "F42", { "sketchPlane" : qUnion([Q0])});
            skLineSegment(sketch, "E310", {"start": v(4, -12.05) * mm, "end": v(0, -12.05) * mm, "construction": true});
            skLineSegment(sketch, "E311", {"start": v(0, -12.05) * mm, "end": v(0, -10.05) * mm, "construction": true});
            skLineSegment(sketch, "E312.bottom", {"start": v(0, -10.05) * mm, "end": v(4, -10.05) * mm});
            skLineSegment(sketch, "E312.top", {"start": v(0, -14) * mm, "end": v(4, -14) * mm});
            skLineSegment(sketch, "E312.left", {"start": v(0, -10.05) * mm, "end": v(0, -14) * mm});
            skLineSegment(sketch, "E312.right", {"start": v(4, -10.05) * mm, "end": v(4, -14) * mm});
            skLineSegment(sketch, "E313", {"start": v(4, -14) * mm, "end": v(0, -14) * mm});
            skLineSegment(sketch, "E314", {"start": v(0, -14) * mm, "end": v(0, -54) * mm});
            skLineSegment(sketch, "E315", {"start": v(0, -54) * mm, "end": v(4, -54) * mm});
            skLineSegment(sketch, "E316", {"start": v(4, -54) * mm, "end": v(4, -58) * mm});
            skLineSegment(sketch, "E317", {"start": v(4, -58) * mm, "end": v(116, -58) * mm});
            skLineSegment(sketch, "E318", {"start": v(116, -58) * mm, "end": v(116, -54) * mm});
            skLineSegment(sketch, "E319", {"start": v(116, -54) * mm, "end": v(120, -54) * mm});
            skLineSegment(sketch, "E320", {"start": v(120, -54) * mm, "end": v(120, -14) * mm});
            skLineSegment(sketch, "E321", {"start": v(120, -14) * mm, "end": v(116, -14) * mm});
            skLineSegment(sketch, "E322", {"start": v(116, -14) * mm, "end": v(116, -10) * mm});
            skLineSegment(sketch, "E323", {"start": v(116, -10) * mm, "end": v(4, -10.05) * mm});
            skSolve(sketch);
        }
        {
            var Q0;
            Q0=makeQuery(id+"F33.opExtrude","CAP_FACE",FACE,{"disambiguationData":[OSD([sQuery(id+"F32.wireOp",EDGE,"E261.bottom"),sQuery(id+"F32.wireOp",EDGE,"E261.top"),sQuery(id+"F32.wireOp",EDGE,"E261.left"),sQuery(id+"F32.wireOp",EDGE,"E261.right")])],"isStart":true});
            var sketch = newSketch(context, id + "F43", { "sketchPlane" : qUnion([Q0])});
            skLineSegment(sketch, "E324.bottom", {"start": v(116, 58) * mm, "end": v(4, 58) * mm});
            skLineSegment(sketch, "E324.top", {"start": v(116, 10) * mm, "end": v(4, 10) * mm});
            skLineSegment(sketch, "E324.left", {"start": v(120, 54) * mm, "end": v(120, 14) * mm});
            skLineSegment(sketch, "E324.right", {"start": v(0, 54) * mm, "end": v(0, 14) * mm});
            skLineSegment(sketch, "E325", {"start": v(0, 54) * mm, "end": v(4, 54) * mm});
            skLineSegment(sketch, "E326", {"start": v(120, 54) * mm, "end": v(116, 54) * mm, "construction": true});
            skLineSegment(sketch, "E327", {"start": v(116, 14) * mm, "end": v(116, 10) * mm});
            skLineSegment(sketch, "E328", {"start": v(116, 10) * mm, "end": v(116, 14) * mm});
            skLineSegment(sketch, "E329", {"start": v(60, 58) * mm, "end": v(60, 66.48) * mm, "construction": true});
            skPoint(sketch, "E329.endSnap0", {"position": v(60, 58) * mm});
            skLineSegment(sketch, "E330", {"start": v(120, 34) * mm, "end": v(125.95, 34) * mm, "construction": true});
            skPoint(sketch, "E330.endSnap0", {"position": v(120, 34) * mm});
            skLineSegment(sketch, "E331.MirrorCS", {"start": v(4, 14) * mm, "end": v(4, 10) * mm});
            skLineSegment(sketch, "E332.MirrorCS", {"start": v(4, 10) * mm, "end": v(4, 14) * mm});
            skLineSegment(sketch, "E333.MirrorCS", {"start": v(0, 14) * mm, "end": v(4, 14) * mm});
            skLineSegment(sketch, "E334.trimOffspring", {"start": v(116, 54) * mm, "end": v(120, 54) * mm});
            skLineSegment(sketch, "E335.trimOffspring", {"start": v(116, 14) * mm, "end": v(120, 14) * mm});
            skLineSegment(sketch, "E336.trimOffspring", {"start": v(116, 54) * mm, "end": v(116, 58) * mm});
            skLineSegment(sketch, "E337.trimOffspring", {"start": v(4, 54) * mm, "end": v(4, 58) * mm});
            skPoint(sketch, "E338.orphan", {"position": v(0, 58) * mm});
            skPoint(sketch, "E339.orphan", {"position": v(120, 58) * mm});
            skPoint(sketch, "E340.orphan", {"position": v(120, 10) * mm});
            skSolve(sketch);
        }
        {
            var Q0;
            Q0 = qSketchRegion(id + "F43", true);
            extrude(context, id + "F44", {"entities" : qUnion([Q0]), "operationType" : NewBodyOperationType.ADD, "oppositeDirection" : true, "depth" : 4.1 * mm});
        }
    });
